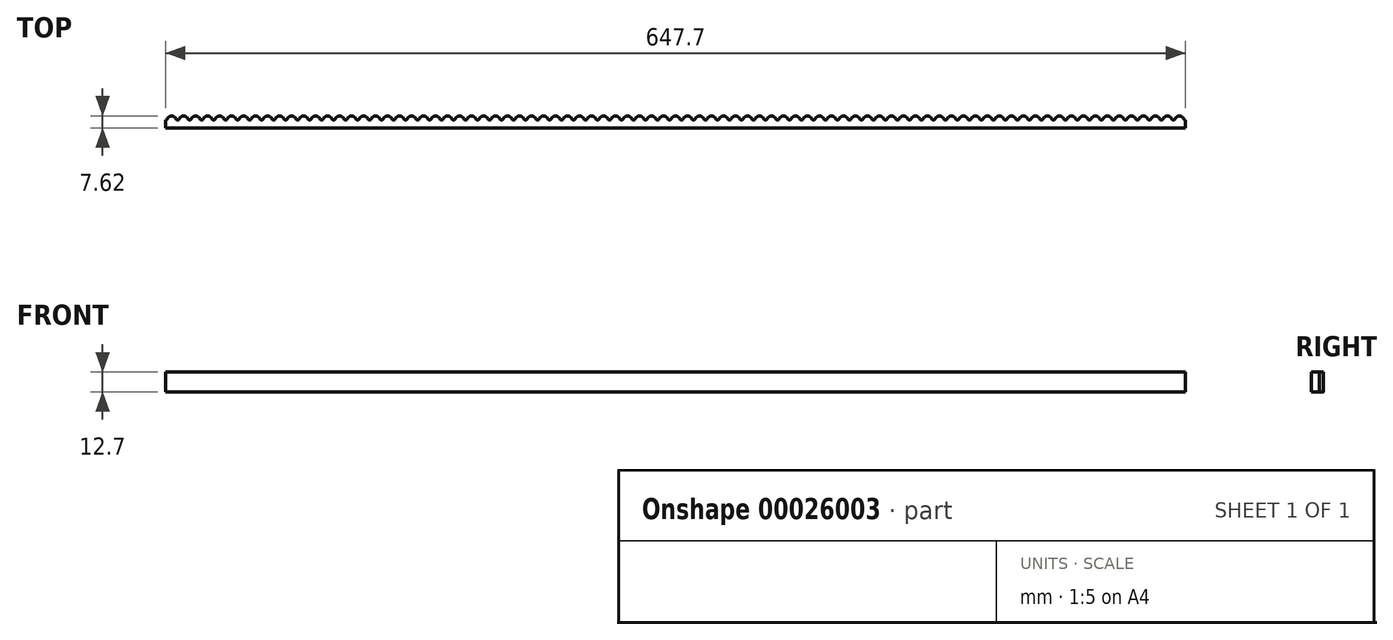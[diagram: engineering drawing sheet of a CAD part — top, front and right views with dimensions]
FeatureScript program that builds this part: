
annotation { "Feature Type Name" : "Feature", "Feature Type Description" : "" }
export const myFeature = defineFeature(function(context is Context, id is Id, definition is map)
    precondition{}
    {
        {
            var Q0;
            Q0=qCreatedBy(makeId("Top.planeOp"),FACE);
            var sketch = newSketch(context, id + "F0", { "sketchPlane" : qUnion([Q0])});
            skLineSegment(sketch, "E0.bottom", {"start": v(0, 0) * mm, "end": v(7.62, 0) * mm});
            skLineSegment(sketch, "E0.top", {"start": v(0, 7.62) * mm, "end": v(7.62, 7.62) * mm, "construction": true});
            skLineSegment(sketch, "E0.left", {"start": v(0, 0) * mm, "end": v(0, 7.62) * mm, "construction": true});
            skLineSegment(sketch, "E0.right", {"start": v(7.62, 0) * mm, "end": v(7.62, 7.62) * mm, "construction": true});
            skLineSegment(sketch, "E1", {"start": v(0, 5.08) * mm, "end": v(7.62, 5.08) * mm, "construction": true});
            skArc(sketch, "E2", {"start": v(0, 5.08) * mm, "mid": v(0.55, 5.21) * mm, "end": v(0.98, 5.58) * mm});
            skArc(sketch, "E3", {"start": v(5.98, 6.5) * mm, "mid": v(3.81, 7.62) * mm, "end": v(1.64, 6.5) * mm});
            skArc(sketch, "E4", {"start": v(6.64, 5.58) * mm, "mid": v(7.07, 5.21) * mm, "end": v(7.62, 5.08) * mm});
            skLineSegment(sketch, "E5", {"start": v(3.8, 5.08) * mm, "end": v(3.8, 7.62) * mm, "construction": true});
            skLineSegment(sketch, "E6", {"start": v(0.98, 5.58) * mm, "end": v(1.64, 6.5) * mm});
            skLineSegment(sketch, "E7", {"start": v(5.98, 6.5) * mm, "end": v(6.64, 5.58) * mm});
            skPoint(sketch, "E8.orphan", {"position": v(1.2, 6.28) * mm});
            skPoint(sketch, "E9.orphan", {"position": v(1.5, 6.28) * mm});
            skPoint(sketch, "E10.orphan", {"position": v(6.12, 6.28) * mm});
            skPoint(sketch, "E11.orphan", {"position": v(6.42, 6.28) * mm});
            skLineSegment(sketch, "E12.1.0.0", {"start": v(7.62, 0) * mm, "end": v(15.24, 0) * mm});
            skArc(sketch, "E12.1.0.1", {"start": v(13.6, 6.5) * mm, "mid": v(11.43, 7.62) * mm, "end": v(9.26, 6.5) * mm});
            skLineSegment(sketch, "E12.1.0.2", {"start": v(13.6, 6.5) * mm, "end": v(14.26, 5.58) * mm});
            skArc(sketch, "E12.1.0.3", {"start": v(7.62, 5.08) * mm, "mid": v(8.17, 5.21) * mm, "end": v(8.6, 5.58) * mm});
            skPoint(sketch, "E12.1.0.4", {"position": v(14.04, 6.28) * mm});
            skLineSegment(sketch, "E12.1.0.5", {"start": v(8.6, 5.58) * mm, "end": v(9.26, 6.5) * mm});
            skArc(sketch, "E12.1.0.6", {"start": v(14.26, 5.58) * mm, "mid": v(14.7, 5.21) * mm, "end": v(15.24, 5.08) * mm});
            skPoint(sketch, "E12.1.0.7", {"position": v(8.82, 6.28) * mm});
            skLineSegment(sketch, "E12.2.0.0", {"start": v(15.24, 0) * mm, "end": v(22.86, 0) * mm});
            skArc(sketch, "E12.2.0.1", {"start": v(21.22, 6.5) * mm, "mid": v(19.05, 7.62) * mm, "end": v(16.88, 6.5) * mm});
            skLineSegment(sketch, "E12.2.0.2", {"start": v(21.22, 6.5) * mm, "end": v(21.88, 5.58) * mm});
            skArc(sketch, "E12.2.0.3", {"start": v(15.24, 5.08) * mm, "mid": v(15.79, 5.21) * mm, "end": v(16.22, 5.58) * mm});
            skPoint(sketch, "E12.2.0.4", {"position": v(21.66, 6.28) * mm});
            skLineSegment(sketch, "E12.2.0.5", {"start": v(16.22, 5.58) * mm, "end": v(16.88, 6.5) * mm});
            skArc(sketch, "E12.2.0.6", {"start": v(21.88, 5.58) * mm, "mid": v(22.31, 5.21) * mm, "end": v(22.86, 5.08) * mm});
            skPoint(sketch, "E12.2.0.7", {"position": v(16.44, 6.28) * mm});
            skLineSegment(sketch, "E12.3.0.0", {"start": v(22.86, 0) * mm, "end": v(30.48, 0) * mm});
            skArc(sketch, "E12.3.0.1", {"start": v(28.84, 6.5) * mm, "mid": v(26.67, 7.62) * mm, "end": v(24.5, 6.5) * mm});
            skLineSegment(sketch, "E12.3.0.2", {"start": v(28.84, 6.5) * mm, "end": v(29.5, 5.58) * mm});
            skArc(sketch, "E12.3.0.3", {"start": v(22.86, 5.08) * mm, "mid": v(23.4, 5.21) * mm, "end": v(23.84, 5.58) * mm});
            skPoint(sketch, "E12.3.0.4", {"position": v(29.28, 6.28) * mm});
            skLineSegment(sketch, "E12.3.0.5", {"start": v(23.84, 5.58) * mm, "end": v(24.5, 6.5) * mm});
            skArc(sketch, "E12.3.0.6", {"start": v(29.5, 5.58) * mm, "mid": v(29.93, 5.21) * mm, "end": v(30.48, 5.08) * mm});
            skPoint(sketch, "E12.3.0.7", {"position": v(24.06, 6.28) * mm});
            skLineSegment(sketch, "E12.4.0.0", {"start": v(30.48, 0) * mm, "end": v(38.1, 0) * mm});
            skArc(sketch, "E12.4.0.1", {"start": v(36.46, 6.5) * mm, "mid": v(34.3, 7.62) * mm, "end": v(32.12, 6.5) * mm});
            skLineSegment(sketch, "E12.4.0.2", {"start": v(36.46, 6.5) * mm, "end": v(37.12, 5.58) * mm});
            skArc(sketch, "E12.4.0.3", {"start": v(30.48, 5.08) * mm, "mid": v(31.03, 5.21) * mm, "end": v(31.46, 5.58) * mm});
            skPoint(sketch, "E12.4.0.4", {"position": v(36.9, 6.28) * mm});
            skLineSegment(sketch, "E12.4.0.5", {"start": v(31.46, 5.58) * mm, "end": v(32.12, 6.5) * mm});
            skArc(sketch, "E12.4.0.6", {"start": v(37.12, 5.58) * mm, "mid": v(37.55, 5.21) * mm, "end": v(38.1, 5.08) * mm});
            skPoint(sketch, "E12.4.0.7", {"position": v(31.68, 6.28) * mm});
            skLineSegment(sketch, "E12.5.0.0", {"start": v(38.1, 0) * mm, "end": v(45.72, 0) * mm});
            skArc(sketch, "E12.5.0.1", {"start": v(44.08, 6.5) * mm, "mid": v(41.91, 7.62) * mm, "end": v(39.74, 6.5) * mm});
            skLineSegment(sketch, "E12.5.0.2", {"start": v(44.08, 6.5) * mm, "end": v(44.74, 5.58) * mm});
            skArc(sketch, "E12.5.0.3", {"start": v(38.1, 5.08) * mm, "mid": v(38.65, 5.21) * mm, "end": v(39.08, 5.58) * mm});
            skPoint(sketch, "E12.5.0.4", {"position": v(44.52, 6.28) * mm});
            skLineSegment(sketch, "E12.5.0.5", {"start": v(39.08, 5.58) * mm, "end": v(39.74, 6.5) * mm});
            skArc(sketch, "E12.5.0.6", {"start": v(44.74, 5.58) * mm, "mid": v(45.17, 5.21) * mm, "end": v(45.72, 5.08) * mm});
            skPoint(sketch, "E12.5.0.7", {"position": v(39.3, 6.28) * mm});
            skLineSegment(sketch, "E12.6.0.0", {"start": v(45.72, 0) * mm, "end": v(53.34, 0) * mm});
            skArc(sketch, "E12.6.0.1", {"start": v(51.7, 6.5) * mm, "mid": v(49.53, 7.62) * mm, "end": v(47.36, 6.5) * mm});
            skLineSegment(sketch, "E12.6.0.2", {"start": v(51.7, 6.5) * mm, "end": v(52.36, 5.58) * mm});
            skArc(sketch, "E12.6.0.3", {"start": v(45.72, 5.08) * mm, "mid": v(46.27, 5.21) * mm, "end": v(46.7, 5.58) * mm});
            skPoint(sketch, "E12.6.0.4", {"position": v(52.14, 6.28) * mm});
            skLineSegment(sketch, "E12.6.0.5", {"start": v(46.7, 5.58) * mm, "end": v(47.36, 6.5) * mm});
            skArc(sketch, "E12.6.0.6", {"start": v(52.36, 5.58) * mm, "mid": v(52.8, 5.21) * mm, "end": v(53.34, 5.08) * mm});
            skPoint(sketch, "E12.6.0.7", {"position": v(46.92, 6.28) * mm});
            skLineSegment(sketch, "E12.7.0.0", {"start": v(53.34, 0) * mm, "end": v(60.96, 0) * mm});
            skArc(sketch, "E12.7.0.1", {"start": v(59.32, 6.5) * mm, "mid": v(57.15, 7.62) * mm, "end": v(54.98, 6.5) * mm});
            skLineSegment(sketch, "E12.7.0.2", {"start": v(59.32, 6.5) * mm, "end": v(59.98, 5.58) * mm});
            skArc(sketch, "E12.7.0.3", {"start": v(53.34, 5.08) * mm, "mid": v(53.89, 5.21) * mm, "end": v(54.32, 5.58) * mm});
            skPoint(sketch, "E12.7.0.4", {"position": v(59.76, 6.28) * mm});
            skLineSegment(sketch, "E12.7.0.5", {"start": v(54.32, 5.58) * mm, "end": v(54.98, 6.5) * mm});
            skArc(sketch, "E12.7.0.6", {"start": v(59.98, 5.58) * mm, "mid": v(60.41, 5.21) * mm, "end": v(60.96, 5.08) * mm});
            skPoint(sketch, "E12.7.0.7", {"position": v(54.54, 6.28) * mm});
            skLineSegment(sketch, "E12.8.0.0", {"start": v(60.96, 0) * mm, "end": v(68.58, 0) * mm});
            skArc(sketch, "E12.8.0.1", {"start": v(66.94, 6.5) * mm, "mid": v(64.77, 7.62) * mm, "end": v(62.6, 6.5) * mm});
            skLineSegment(sketch, "E12.8.0.2", {"start": v(66.94, 6.5) * mm, "end": v(67.6, 5.58) * mm});
            skArc(sketch, "E12.8.0.3", {"start": v(60.96, 5.08) * mm, "mid": v(61.5, 5.21) * mm, "end": v(61.94, 5.58) * mm});
            skPoint(sketch, "E12.8.0.4", {"position": v(67.38, 6.28) * mm});
            skLineSegment(sketch, "E12.8.0.5", {"start": v(61.94, 5.58) * mm, "end": v(62.6, 6.5) * mm});
            skArc(sketch, "E12.8.0.6", {"start": v(67.6, 5.58) * mm, "mid": v(68.03, 5.21) * mm, "end": v(68.58, 5.08) * mm});
            skPoint(sketch, "E12.8.0.7", {"position": v(62.16, 6.28) * mm});
            skLineSegment(sketch, "E12.9.0.0", {"start": v(68.58, 0) * mm, "end": v(76.2, 0) * mm});
            skArc(sketch, "E12.9.0.1", {"start": v(74.56, 6.5) * mm, "mid": v(72.4, 7.62) * mm, "end": v(70.22, 6.5) * mm});
            skLineSegment(sketch, "E12.9.0.2", {"start": v(74.56, 6.5) * mm, "end": v(75.22, 5.58) * mm});
            skArc(sketch, "E12.9.0.3", {"start": v(68.58, 5.08) * mm, "mid": v(69.13, 5.21) * mm, "end": v(69.56, 5.58) * mm});
            skPoint(sketch, "E12.9.0.4", {"position": v(75, 6.28) * mm});
            skLineSegment(sketch, "E12.9.0.5", {"start": v(69.56, 5.58) * mm, "end": v(70.22, 6.5) * mm});
            skArc(sketch, "E12.9.0.6", {"start": v(75.22, 5.58) * mm, "mid": v(75.65, 5.21) * mm, "end": v(76.2, 5.08) * mm});
            skPoint(sketch, "E12.9.0.7", {"position": v(69.78, 6.28) * mm});
            skLineSegment(sketch, "E12.10.0.0", {"start": v(76.2, 0) * mm, "end": v(83.82, 0) * mm});
            skArc(sketch, "E12.10.0.1", {"start": v(82.18, 6.5) * mm, "mid": v(80.01, 7.62) * mm, "end": v(77.84, 6.5) * mm});
            skLineSegment(sketch, "E12.10.0.2", {"start": v(82.18, 6.5) * mm, "end": v(82.84, 5.58) * mm});
            skArc(sketch, "E12.10.0.3", {"start": v(76.2, 5.08) * mm, "mid": v(76.75, 5.21) * mm, "end": v(77.18, 5.58) * mm});
            skPoint(sketch, "E12.10.0.4", {"position": v(82.62, 6.28) * mm});
            skLineSegment(sketch, "E12.10.0.5", {"start": v(77.18, 5.58) * mm, "end": v(77.84, 6.5) * mm});
            skArc(sketch, "E12.10.0.6", {"start": v(82.84, 5.58) * mm, "mid": v(83.27, 5.21) * mm, "end": v(83.82, 5.08) * mm});
            skPoint(sketch, "E12.10.0.7", {"position": v(77.4, 6.28) * mm});
            skLineSegment(sketch, "E12.11.0.0", {"start": v(83.82, 0) * mm, "end": v(91.44, 0) * mm});
            skArc(sketch, "E12.11.0.1", {"start": v(89.8, 6.5) * mm, "mid": v(87.63, 7.62) * mm, "end": v(85.46, 6.5) * mm});
            skLineSegment(sketch, "E12.11.0.2", {"start": v(89.8, 6.5) * mm, "end": v(90.46, 5.58) * mm});
            skArc(sketch, "E12.11.0.3", {"start": v(83.82, 5.08) * mm, "mid": v(84.37, 5.21) * mm, "end": v(84.8, 5.58) * mm});
            skPoint(sketch, "E12.11.0.4", {"position": v(90.24, 6.28) * mm});
            skLineSegment(sketch, "E12.11.0.5", {"start": v(84.8, 5.58) * mm, "end": v(85.46, 6.5) * mm});
            skArc(sketch, "E12.11.0.6", {"start": v(90.46, 5.58) * mm, "mid": v(90.9, 5.21) * mm, "end": v(91.44, 5.08) * mm});
            skPoint(sketch, "E12.11.0.7", {"position": v(85.02, 6.28) * mm});
            skLineSegment(sketch, "E12.12.0.0", {"start": v(91.44, 0) * mm, "end": v(99.06, 0) * mm});
            skArc(sketch, "E12.12.0.1", {"start": v(97.42, 6.5) * mm, "mid": v(95.25, 7.62) * mm, "end": v(93.08, 6.5) * mm});
            skLineSegment(sketch, "E12.12.0.2", {"start": v(97.42, 6.5) * mm, "end": v(98.08, 5.58) * mm});
            skArc(sketch, "E12.12.0.3", {"start": v(91.44, 5.08) * mm, "mid": v(91.99, 5.21) * mm, "end": v(92.42, 5.58) * mm});
            skPoint(sketch, "E12.12.0.4", {"position": v(97.86, 6.28) * mm});
            skLineSegment(sketch, "E12.12.0.5", {"start": v(92.42, 5.58) * mm, "end": v(93.08, 6.5) * mm});
            skArc(sketch, "E12.12.0.6", {"start": v(98.08, 5.58) * mm, "mid": v(98.51, 5.21) * mm, "end": v(99.06, 5.08) * mm});
            skPoint(sketch, "E12.12.0.7", {"position": v(92.64, 6.28) * mm});
            skLineSegment(sketch, "E12.13.0.0", {"start": v(99.06, 0) * mm, "end": v(106.68, 0) * mm});
            skArc(sketch, "E12.13.0.1", {"start": v(105.04, 6.5) * mm, "mid": v(102.87, 7.62) * mm, "end": v(100.7, 6.5) * mm});
            skLineSegment(sketch, "E12.13.0.2", {"start": v(105.04, 6.5) * mm, "end": v(105.7, 5.58) * mm});
            skArc(sketch, "E12.13.0.3", {"start": v(99.06, 5.08) * mm, "mid": v(99.6, 5.21) * mm, "end": v(100.04, 5.58) * mm});
            skPoint(sketch, "E12.13.0.4", {"position": v(105.48, 6.28) * mm});
            skLineSegment(sketch, "E12.13.0.5", {"start": v(100.04, 5.58) * mm, "end": v(100.7, 6.5) * mm});
            skArc(sketch, "E12.13.0.6", {"start": v(105.7, 5.58) * mm, "mid": v(106.13, 5.21) * mm, "end": v(106.68, 5.08) * mm});
            skPoint(sketch, "E12.13.0.7", {"position": v(100.26, 6.28) * mm});
            skLineSegment(sketch, "E12.14.0.0", {"start": v(106.68, 0) * mm, "end": v(114.3, 0) * mm});
            skArc(sketch, "E12.14.0.1", {"start": v(112.66, 6.5) * mm, "mid": v(110.5, 7.62) * mm, "end": v(108.32, 6.5) * mm});
            skLineSegment(sketch, "E12.14.0.2", {"start": v(112.66, 6.5) * mm, "end": v(113.32, 5.58) * mm});
            skArc(sketch, "E12.14.0.3", {"start": v(106.68, 5.08) * mm, "mid": v(107.23, 5.21) * mm, "end": v(107.66, 5.58) * mm});
            skPoint(sketch, "E12.14.0.4", {"position": v(113.1, 6.28) * mm});
            skLineSegment(sketch, "E12.14.0.5", {"start": v(107.66, 5.58) * mm, "end": v(108.32, 6.5) * mm});
            skArc(sketch, "E12.14.0.6", {"start": v(113.32, 5.58) * mm, "mid": v(113.75, 5.21) * mm, "end": v(114.3, 5.08) * mm});
            skPoint(sketch, "E12.14.0.7", {"position": v(107.88, 6.28) * mm});
            skLineSegment(sketch, "E12.15.0.0", {"start": v(114.3, 0) * mm, "end": v(121.92, 0) * mm});
            skArc(sketch, "E12.15.0.1", {"start": v(120.28, 6.5) * mm, "mid": v(118.11, 7.62) * mm, "end": v(115.94, 6.5) * mm});
            skLineSegment(sketch, "E12.15.0.2", {"start": v(120.28, 6.5) * mm, "end": v(120.94, 5.58) * mm});
            skArc(sketch, "E12.15.0.3", {"start": v(114.3, 5.08) * mm, "mid": v(114.85, 5.21) * mm, "end": v(115.28, 5.58) * mm});
            skPoint(sketch, "E12.15.0.4", {"position": v(120.72, 6.28) * mm});
            skLineSegment(sketch, "E12.15.0.5", {"start": v(115.28, 5.58) * mm, "end": v(115.94, 6.5) * mm});
            skArc(sketch, "E12.15.0.6", {"start": v(120.94, 5.58) * mm, "mid": v(121.37, 5.21) * mm, "end": v(121.92, 5.08) * mm});
            skPoint(sketch, "E12.15.0.7", {"position": v(115.5, 6.28) * mm});
            skLineSegment(sketch, "E12.16.0.0", {"start": v(121.92, 0) * mm, "end": v(129.54, 0) * mm});
            skArc(sketch, "E12.16.0.1", {"start": v(127.9, 6.5) * mm, "mid": v(125.73, 7.62) * mm, "end": v(123.56, 6.5) * mm});
            skLineSegment(sketch, "E12.16.0.2", {"start": v(127.9, 6.5) * mm, "end": v(128.56, 5.58) * mm});
            skArc(sketch, "E12.16.0.3", {"start": v(121.92, 5.08) * mm, "mid": v(122.47, 5.21) * mm, "end": v(122.9, 5.58) * mm});
            skPoint(sketch, "E12.16.0.4", {"position": v(128.34, 6.28) * mm});
            skLineSegment(sketch, "E12.16.0.5", {"start": v(122.9, 5.58) * mm, "end": v(123.56, 6.5) * mm});
            skArc(sketch, "E12.16.0.6", {"start": v(128.56, 5.58) * mm, "mid": v(129, 5.21) * mm, "end": v(129.54, 5.08) * mm});
            skPoint(sketch, "E12.16.0.7", {"position": v(123.12, 6.28) * mm});
            skLineSegment(sketch, "E12.17.0.0", {"start": v(129.54, 0) * mm, "end": v(137.16, 0) * mm});
            skArc(sketch, "E12.17.0.1", {"start": v(135.52, 6.5) * mm, "mid": v(133.35, 7.62) * mm, "end": v(131.18, 6.5) * mm});
            skLineSegment(sketch, "E12.17.0.2", {"start": v(135.52, 6.5) * mm, "end": v(136.18, 5.58) * mm});
            skArc(sketch, "E12.17.0.3", {"start": v(129.54, 5.08) * mm, "mid": v(130.09, 5.21) * mm, "end": v(130.52, 5.58) * mm});
            skPoint(sketch, "E12.17.0.4", {"position": v(135.96, 6.28) * mm});
            skLineSegment(sketch, "E12.17.0.5", {"start": v(130.52, 5.58) * mm, "end": v(131.18, 6.5) * mm});
            skArc(sketch, "E12.17.0.6", {"start": v(136.18, 5.58) * mm, "mid": v(136.61, 5.21) * mm, "end": v(137.16, 5.08) * mm});
            skPoint(sketch, "E12.17.0.7", {"position": v(130.74, 6.28) * mm});
            skLineSegment(sketch, "E12.18.0.0", {"start": v(137.16, 0) * mm, "end": v(144.78, 0) * mm});
            skArc(sketch, "E12.18.0.1", {"start": v(143.14, 6.5) * mm, "mid": v(140.97, 7.62) * mm, "end": v(138.8, 6.5) * mm});
            skLineSegment(sketch, "E12.18.0.2", {"start": v(143.14, 6.5) * mm, "end": v(143.8, 5.58) * mm});
            skArc(sketch, "E12.18.0.3", {"start": v(137.16, 5.08) * mm, "mid": v(137.7, 5.21) * mm, "end": v(138.14, 5.58) * mm});
            skPoint(sketch, "E12.18.0.4", {"position": v(143.58, 6.28) * mm});
            skLineSegment(sketch, "E12.18.0.5", {"start": v(138.14, 5.58) * mm, "end": v(138.8, 6.5) * mm});
            skArc(sketch, "E12.18.0.6", {"start": v(143.8, 5.58) * mm, "mid": v(144.23, 5.21) * mm, "end": v(144.78, 5.08) * mm});
            skPoint(sketch, "E12.18.0.7", {"position": v(138.36, 6.28) * mm});
            skLineSegment(sketch, "E12.19.0.0", {"start": v(144.78, 0) * mm, "end": v(152.4, 0) * mm});
            skArc(sketch, "E12.19.0.1", {"start": v(150.76, 6.5) * mm, "mid": v(148.6, 7.62) * mm, "end": v(146.42, 6.5) * mm});
            skLineSegment(sketch, "E12.19.0.2", {"start": v(150.76, 6.5) * mm, "end": v(151.42, 5.58) * mm});
            skArc(sketch, "E12.19.0.3", {"start": v(144.78, 5.08) * mm, "mid": v(145.33, 5.21) * mm, "end": v(145.76, 5.58) * mm});
            skPoint(sketch, "E12.19.0.4", {"position": v(151.2, 6.28) * mm});
            skLineSegment(sketch, "E12.19.0.5", {"start": v(145.76, 5.58) * mm, "end": v(146.42, 6.5) * mm});
            skArc(sketch, "E12.19.0.6", {"start": v(151.42, 5.58) * mm, "mid": v(151.85, 5.21) * mm, "end": v(152.4, 5.08) * mm});
            skPoint(sketch, "E12.19.0.7", {"position": v(145.98, 6.28) * mm});
            skLineSegment(sketch, "E12.direction1", {"start": v(0, 0) * mm, "end": v(7.62, 0) * mm, "construction": true});
            skLineSegment(sketch, "E13.0.20.0", {"start": v(152.4, 0) * mm, "end": v(160.02, 0) * mm});
            skArc(sketch, "E13.3.20.0", {"start": v(158.38, 6.5) * mm, "mid": v(156.21, 7.62) * mm, "end": v(154.04, 6.5) * mm});
            skLineSegment(sketch, "E13.7.20.0", {"start": v(158.38, 6.5) * mm, "end": v(159.04, 5.58) * mm});
            skArc(sketch, "E13.10.20.0", {"start": v(152.4, 5.08) * mm, "mid": v(152.95, 5.21) * mm, "end": v(153.38, 5.58) * mm});
            skPoint(sketch, "E13.14.20.0", {"position": v(158.82, 6.28) * mm});
            skLineSegment(sketch, "E13.15.20.0", {"start": v(153.38, 5.58) * mm, "end": v(154.04, 6.5) * mm});
            skArc(sketch, "E13.18.20.0", {"start": v(159.04, 5.58) * mm, "mid": v(159.47, 5.21) * mm, "end": v(160.02, 5.08) * mm});
            skPoint(sketch, "E13.22.20.0", {"position": v(153.6, 6.28) * mm});
            skLineSegment(sketch, "E13.0.21.0", {"start": v(160.02, 0) * mm, "end": v(167.64, 0) * mm});
            skArc(sketch, "E13.3.21.0", {"start": v(166, 6.5) * mm, "mid": v(163.83, 7.62) * mm, "end": v(161.66, 6.5) * mm});
            skLineSegment(sketch, "E13.7.21.0", {"start": v(166, 6.5) * mm, "end": v(166.66, 5.58) * mm});
            skArc(sketch, "E13.10.21.0", {"start": v(160.02, 5.08) * mm, "mid": v(160.57, 5.21) * mm, "end": v(161, 5.58) * mm});
            skPoint(sketch, "E13.14.21.0", {"position": v(166.44, 6.28) * mm});
            skLineSegment(sketch, "E13.15.21.0", {"start": v(161, 5.58) * mm, "end": v(161.66, 6.5) * mm});
            skArc(sketch, "E13.18.21.0", {"start": v(166.66, 5.58) * mm, "mid": v(167.1, 5.21) * mm, "end": v(167.64, 5.08) * mm});
            skPoint(sketch, "E13.22.21.0", {"position": v(161.22, 6.28) * mm});
            skLineSegment(sketch, "E13.0.22.0", {"start": v(167.64, 0) * mm, "end": v(175.26, 0) * mm});
            skArc(sketch, "E13.3.22.0", {"start": v(173.62, 6.5) * mm, "mid": v(171.45, 7.62) * mm, "end": v(169.28, 6.5) * mm});
            skLineSegment(sketch, "E13.7.22.0", {"start": v(173.62, 6.5) * mm, "end": v(174.28, 5.58) * mm});
            skArc(sketch, "E13.10.22.0", {"start": v(167.64, 5.08) * mm, "mid": v(168.19, 5.21) * mm, "end": v(168.62, 5.58) * mm});
            skPoint(sketch, "E13.14.22.0", {"position": v(174.06, 6.28) * mm});
            skLineSegment(sketch, "E13.15.22.0", {"start": v(168.62, 5.58) * mm, "end": v(169.28, 6.5) * mm});
            skArc(sketch, "E13.18.22.0", {"start": v(174.28, 5.58) * mm, "mid": v(174.71, 5.21) * mm, "end": v(175.26, 5.08) * mm});
            skPoint(sketch, "E13.22.22.0", {"position": v(168.84, 6.28) * mm});
            skLineSegment(sketch, "E13.0.23.0", {"start": v(175.26, 0) * mm, "end": v(182.88, 0) * mm});
            skArc(sketch, "E13.3.23.0", {"start": v(181.24, 6.5) * mm, "mid": v(179.07, 7.62) * mm, "end": v(176.9, 6.5) * mm});
            skLineSegment(sketch, "E13.7.23.0", {"start": v(181.24, 6.5) * mm, "end": v(181.9, 5.58) * mm});
            skArc(sketch, "E13.10.23.0", {"start": v(175.26, 5.08) * mm, "mid": v(175.8, 5.21) * mm, "end": v(176.24, 5.58) * mm});
            skPoint(sketch, "E13.14.23.0", {"position": v(181.68, 6.28) * mm});
            skLineSegment(sketch, "E13.15.23.0", {"start": v(176.24, 5.58) * mm, "end": v(176.9, 6.5) * mm});
            skArc(sketch, "E13.18.23.0", {"start": v(181.9, 5.58) * mm, "mid": v(182.33, 5.21) * mm, "end": v(182.88, 5.08) * mm});
            skPoint(sketch, "E13.22.23.0", {"position": v(176.46, 6.28) * mm});
            skLineSegment(sketch, "E13.0.24.0", {"start": v(182.88, 0) * mm, "end": v(190.5, 0) * mm});
            skArc(sketch, "E13.3.24.0", {"start": v(188.86, 6.5) * mm, "mid": v(186.7, 7.62) * mm, "end": v(184.52, 6.5) * mm});
            skLineSegment(sketch, "E13.7.24.0", {"start": v(188.86, 6.5) * mm, "end": v(189.52, 5.58) * mm});
            skArc(sketch, "E13.10.24.0", {"start": v(182.88, 5.08) * mm, "mid": v(183.43, 5.21) * mm, "end": v(183.86, 5.58) * mm});
            skPoint(sketch, "E13.14.24.0", {"position": v(189.3, 6.28) * mm});
            skLineSegment(sketch, "E13.15.24.0", {"start": v(183.86, 5.58) * mm, "end": v(184.52, 6.5) * mm});
            skArc(sketch, "E13.18.24.0", {"start": v(189.52, 5.58) * mm, "mid": v(189.95, 5.21) * mm, "end": v(190.5, 5.08) * mm});
            skPoint(sketch, "E13.22.24.0", {"position": v(184.08, 6.28) * mm});
            skLineSegment(sketch, "E13.0.25.0", {"start": v(190.5, 0) * mm, "end": v(198.12, 0) * mm});
            skArc(sketch, "E13.3.25.0", {"start": v(196.48, 6.5) * mm, "mid": v(194.3, 7.62) * mm, "end": v(192.14, 6.5) * mm});
            skLineSegment(sketch, "E13.7.25.0", {"start": v(196.48, 6.5) * mm, "end": v(197.14, 5.58) * mm});
            skArc(sketch, "E13.10.25.0", {"start": v(190.5, 5.08) * mm, "mid": v(191.05, 5.21) * mm, "end": v(191.48, 5.58) * mm});
            skPoint(sketch, "E13.14.25.0", {"position": v(196.92, 6.28) * mm});
            skLineSegment(sketch, "E13.15.25.0", {"start": v(191.48, 5.58) * mm, "end": v(192.14, 6.5) * mm});
            skArc(sketch, "E13.18.25.0", {"start": v(197.14, 5.58) * mm, "mid": v(197.57, 5.21) * mm, "end": v(198.12, 5.08) * mm});
            skPoint(sketch, "E13.22.25.0", {"position": v(191.7, 6.28) * mm});
            skLineSegment(sketch, "E13.0.26.0", {"start": v(198.12, 0) * mm, "end": v(205.74, 0) * mm});
            skArc(sketch, "E13.3.26.0", {"start": v(204.1, 6.5) * mm, "mid": v(201.93, 7.62) * mm, "end": v(199.76, 6.5) * mm});
            skLineSegment(sketch, "E13.7.26.0", {"start": v(204.1, 6.5) * mm, "end": v(204.76, 5.58) * mm});
            skArc(sketch, "E13.10.26.0", {"start": v(198.12, 5.08) * mm, "mid": v(198.67, 5.21) * mm, "end": v(199.1, 5.58) * mm});
            skPoint(sketch, "E13.14.26.0", {"position": v(204.54, 6.28) * mm});
            skLineSegment(sketch, "E13.15.26.0", {"start": v(199.1, 5.58) * mm, "end": v(199.76, 6.5) * mm});
            skArc(sketch, "E13.18.26.0", {"start": v(204.76, 5.58) * mm, "mid": v(205.2, 5.21) * mm, "end": v(205.74, 5.08) * mm});
            skPoint(sketch, "E13.22.26.0", {"position": v(199.32, 6.28) * mm});
            skLineSegment(sketch, "E13.0.27.0", {"start": v(205.74, 0) * mm, "end": v(213.36, 0) * mm});
            skArc(sketch, "E13.3.27.0", {"start": v(211.72, 6.5) * mm, "mid": v(209.55, 7.62) * mm, "end": v(207.38, 6.5) * mm});
            skLineSegment(sketch, "E13.7.27.0", {"start": v(211.72, 6.5) * mm, "end": v(212.38, 5.58) * mm});
            skArc(sketch, "E13.10.27.0", {"start": v(205.74, 5.08) * mm, "mid": v(206.29, 5.21) * mm, "end": v(206.72, 5.58) * mm});
            skPoint(sketch, "E13.14.27.0", {"position": v(212.16, 6.28) * mm});
            skLineSegment(sketch, "E13.15.27.0", {"start": v(206.72, 5.58) * mm, "end": v(207.38, 6.5) * mm});
            skArc(sketch, "E13.18.27.0", {"start": v(212.38, 5.58) * mm, "mid": v(212.81, 5.21) * mm, "end": v(213.36, 5.08) * mm});
            skPoint(sketch, "E13.22.27.0", {"position": v(206.94, 6.28) * mm});
            skLineSegment(sketch, "E13.0.28.0", {"start": v(213.36, 0) * mm, "end": v(220.98, 0) * mm});
            skArc(sketch, "E13.3.28.0", {"start": v(219.34, 6.5) * mm, "mid": v(217.17, 7.62) * mm, "end": v(215, 6.5) * mm});
            skLineSegment(sketch, "E13.7.28.0", {"start": v(219.34, 6.5) * mm, "end": v(220, 5.58) * mm});
            skArc(sketch, "E13.10.28.0", {"start": v(213.36, 5.08) * mm, "mid": v(213.9, 5.21) * mm, "end": v(214.34, 5.58) * mm});
            skPoint(sketch, "E13.14.28.0", {"position": v(219.78, 6.28) * mm});
            skLineSegment(sketch, "E13.15.28.0", {"start": v(214.34, 5.58) * mm, "end": v(215, 6.5) * mm});
            skArc(sketch, "E13.18.28.0", {"start": v(220, 5.58) * mm, "mid": v(220.43, 5.21) * mm, "end": v(220.98, 5.08) * mm});
            skPoint(sketch, "E13.22.28.0", {"position": v(214.56, 6.28) * mm});
            skLineSegment(sketch, "E13.0.29.0", {"start": v(220.98, 0) * mm, "end": v(228.6, 0) * mm});
            skArc(sketch, "E13.3.29.0", {"start": v(226.96, 6.5) * mm, "mid": v(224.8, 7.62) * mm, "end": v(222.62, 6.5) * mm});
            skLineSegment(sketch, "E13.7.29.0", {"start": v(226.96, 6.5) * mm, "end": v(227.62, 5.58) * mm});
            skArc(sketch, "E13.10.29.0", {"start": v(220.98, 5.08) * mm, "mid": v(221.53, 5.21) * mm, "end": v(221.96, 5.58) * mm});
            skPoint(sketch, "E13.14.29.0", {"position": v(227.4, 6.28) * mm});
            skLineSegment(sketch, "E13.15.29.0", {"start": v(221.96, 5.58) * mm, "end": v(222.62, 6.5) * mm});
            skArc(sketch, "E13.18.29.0", {"start": v(227.62, 5.58) * mm, "mid": v(228.05, 5.21) * mm, "end": v(228.6, 5.08) * mm});
            skPoint(sketch, "E13.22.29.0", {"position": v(222.18, 6.28) * mm});
            skLineSegment(sketch, "E13.0.30.0", {"start": v(228.6, 0) * mm, "end": v(236.22, 0) * mm});
            skArc(sketch, "E13.3.30.0", {"start": v(234.58, 6.5) * mm, "mid": v(232.4, 7.62) * mm, "end": v(230.24, 6.5) * mm});
            skLineSegment(sketch, "E13.7.30.0", {"start": v(234.58, 6.5) * mm, "end": v(235.24, 5.58) * mm});
            skArc(sketch, "E13.10.30.0", {"start": v(228.6, 5.08) * mm, "mid": v(229.15, 5.21) * mm, "end": v(229.58, 5.58) * mm});
            skPoint(sketch, "E13.14.30.0", {"position": v(235.02, 6.28) * mm});
            skLineSegment(sketch, "E13.15.30.0", {"start": v(229.58, 5.58) * mm, "end": v(230.24, 6.5) * mm});
            skArc(sketch, "E13.18.30.0", {"start": v(235.24, 5.58) * mm, "mid": v(235.67, 5.21) * mm, "end": v(236.22, 5.08) * mm});
            skPoint(sketch, "E13.22.30.0", {"position": v(229.8, 6.28) * mm});
            skLineSegment(sketch, "E13.0.31.0", {"start": v(236.22, 0) * mm, "end": v(243.84, 0) * mm});
            skArc(sketch, "E13.3.31.0", {"start": v(242.2, 6.5) * mm, "mid": v(240.03, 7.62) * mm, "end": v(237.86, 6.5) * mm});
            skLineSegment(sketch, "E13.7.31.0", {"start": v(242.2, 6.5) * mm, "end": v(242.86, 5.58) * mm});
            skArc(sketch, "E13.10.31.0", {"start": v(236.22, 5.08) * mm, "mid": v(236.77, 5.21) * mm, "end": v(237.2, 5.58) * mm});
            skPoint(sketch, "E13.14.31.0", {"position": v(242.64, 6.28) * mm});
            skLineSegment(sketch, "E13.15.31.0", {"start": v(237.2, 5.58) * mm, "end": v(237.86, 6.5) * mm});
            skArc(sketch, "E13.18.31.0", {"start": v(242.86, 5.58) * mm, "mid": v(243.3, 5.21) * mm, "end": v(243.84, 5.08) * mm});
            skPoint(sketch, "E13.22.31.0", {"position": v(237.42, 6.28) * mm});
            skLineSegment(sketch, "E13.0.32.0", {"start": v(243.84, 0) * mm, "end": v(251.46, 0) * mm});
            skArc(sketch, "E13.3.32.0", {"start": v(249.82, 6.5) * mm, "mid": v(247.65, 7.62) * mm, "end": v(245.48, 6.5) * mm});
            skLineSegment(sketch, "E13.7.32.0", {"start": v(249.82, 6.5) * mm, "end": v(250.48, 5.58) * mm});
            skArc(sketch, "E13.10.32.0", {"start": v(243.84, 5.08) * mm, "mid": v(244.39, 5.21) * mm, "end": v(244.82, 5.58) * mm});
            skPoint(sketch, "E13.14.32.0", {"position": v(250.26, 6.28) * mm});
            skLineSegment(sketch, "E13.15.32.0", {"start": v(244.82, 5.58) * mm, "end": v(245.48, 6.5) * mm});
            skArc(sketch, "E13.18.32.0", {"start": v(250.48, 5.58) * mm, "mid": v(250.91, 5.21) * mm, "end": v(251.46, 5.08) * mm});
            skPoint(sketch, "E13.22.32.0", {"position": v(245.04, 6.28) * mm});
            skLineSegment(sketch, "E13.0.33.0", {"start": v(251.46, 0) * mm, "end": v(259.08, 0) * mm});
            skArc(sketch, "E13.3.33.0", {"start": v(257.44, 6.5) * mm, "mid": v(255.27, 7.62) * mm, "end": v(253.1, 6.5) * mm});
            skLineSegment(sketch, "E13.7.33.0", {"start": v(257.44, 6.5) * mm, "end": v(258.1, 5.58) * mm});
            skArc(sketch, "E13.10.33.0", {"start": v(251.46, 5.08) * mm, "mid": v(252, 5.21) * mm, "end": v(252.44, 5.58) * mm});
            skPoint(sketch, "E13.14.33.0", {"position": v(257.88, 6.28) * mm});
            skLineSegment(sketch, "E13.15.33.0", {"start": v(252.44, 5.58) * mm, "end": v(253.1, 6.5) * mm});
            skArc(sketch, "E13.18.33.0", {"start": v(258.1, 5.58) * mm, "mid": v(258.53, 5.21) * mm, "end": v(259.08, 5.08) * mm});
            skPoint(sketch, "E13.22.33.0", {"position": v(252.66, 6.28) * mm});
            skLineSegment(sketch, "E13.0.34.0", {"start": v(259.08, 0) * mm, "end": v(266.7, 0) * mm});
            skArc(sketch, "E13.3.34.0", {"start": v(265.06, 6.5) * mm, "mid": v(262.9, 7.62) * mm, "end": v(260.72, 6.5) * mm});
            skLineSegment(sketch, "E13.7.34.0", {"start": v(265.06, 6.5) * mm, "end": v(265.72, 5.58) * mm});
            skArc(sketch, "E13.10.34.0", {"start": v(259.08, 5.08) * mm, "mid": v(259.63, 5.21) * mm, "end": v(260.06, 5.58) * mm});
            skPoint(sketch, "E13.14.34.0", {"position": v(265.5, 6.28) * mm});
            skLineSegment(sketch, "E13.15.34.0", {"start": v(260.06, 5.58) * mm, "end": v(260.72, 6.5) * mm});
            skArc(sketch, "E13.18.34.0", {"start": v(265.72, 5.58) * mm, "mid": v(266.15, 5.21) * mm, "end": v(266.7, 5.08) * mm});
            skPoint(sketch, "E13.22.34.0", {"position": v(260.28, 6.28) * mm});
            skLineSegment(sketch, "E13.0.35.0", {"start": v(266.7, 0) * mm, "end": v(274.32, 0) * mm});
            skArc(sketch, "E13.3.35.0", {"start": v(272.68, 6.5) * mm, "mid": v(270.51, 7.62) * mm, "end": v(268.34, 6.5) * mm});
            skLineSegment(sketch, "E13.7.35.0", {"start": v(272.68, 6.5) * mm, "end": v(273.34, 5.58) * mm});
            skArc(sketch, "E13.10.35.0", {"start": v(266.7, 5.08) * mm, "mid": v(267.25, 5.21) * mm, "end": v(267.68, 5.58) * mm});
            skPoint(sketch, "E13.14.35.0", {"position": v(273.12, 6.28) * mm});
            skLineSegment(sketch, "E13.15.35.0", {"start": v(267.68, 5.58) * mm, "end": v(268.34, 6.5) * mm});
            skArc(sketch, "E13.18.35.0", {"start": v(273.34, 5.58) * mm, "mid": v(273.77, 5.21) * mm, "end": v(274.32, 5.08) * mm});
            skPoint(sketch, "E13.22.35.0", {"position": v(267.9, 6.28) * mm});
            skLineSegment(sketch, "E13.0.36.0", {"start": v(274.32, 0) * mm, "end": v(281.94, 0) * mm});
            skArc(sketch, "E13.3.36.0", {"start": v(280.3, 6.5) * mm, "mid": v(278.13, 7.62) * mm, "end": v(275.96, 6.5) * mm});
            skLineSegment(sketch, "E13.7.36.0", {"start": v(280.3, 6.5) * mm, "end": v(280.96, 5.58) * mm});
            skArc(sketch, "E13.10.36.0", {"start": v(274.32, 5.08) * mm, "mid": v(274.87, 5.21) * mm, "end": v(275.3, 5.58) * mm});
            skPoint(sketch, "E13.14.36.0", {"position": v(280.74, 6.28) * mm});
            skLineSegment(sketch, "E13.15.36.0", {"start": v(275.3, 5.58) * mm, "end": v(275.96, 6.5) * mm});
            skArc(sketch, "E13.18.36.0", {"start": v(280.96, 5.58) * mm, "mid": v(281.4, 5.21) * mm, "end": v(281.94, 5.08) * mm});
            skPoint(sketch, "E13.22.36.0", {"position": v(275.52, 6.28) * mm});
            skLineSegment(sketch, "E13.0.37.0", {"start": v(281.94, 0) * mm, "end": v(289.56, 0) * mm});
            skArc(sketch, "E13.3.37.0", {"start": v(287.92, 6.5) * mm, "mid": v(285.75, 7.62) * mm, "end": v(283.58, 6.5) * mm});
            skLineSegment(sketch, "E13.7.37.0", {"start": v(287.92, 6.5) * mm, "end": v(288.58, 5.58) * mm});
            skArc(sketch, "E13.10.37.0", {"start": v(281.94, 5.08) * mm, "mid": v(282.49, 5.21) * mm, "end": v(282.92, 5.58) * mm});
            skPoint(sketch, "E13.14.37.0", {"position": v(288.36, 6.28) * mm});
            skLineSegment(sketch, "E13.15.37.0", {"start": v(282.92, 5.58) * mm, "end": v(283.58, 6.5) * mm});
            skArc(sketch, "E13.18.37.0", {"start": v(288.58, 5.58) * mm, "mid": v(289.01, 5.21) * mm, "end": v(289.56, 5.08) * mm});
            skPoint(sketch, "E13.22.37.0", {"position": v(283.14, 6.28) * mm});
            skLineSegment(sketch, "E13.0.38.0", {"start": v(289.56, 0) * mm, "end": v(297.18, 0) * mm});
            skArc(sketch, "E13.3.38.0", {"start": v(295.54, 6.5) * mm, "mid": v(293.37, 7.62) * mm, "end": v(291.2, 6.5) * mm});
            skLineSegment(sketch, "E13.7.38.0", {"start": v(295.54, 6.5) * mm, "end": v(296.2, 5.58) * mm});
            skArc(sketch, "E13.10.38.0", {"start": v(289.56, 5.08) * mm, "mid": v(290.1, 5.21) * mm, "end": v(290.54, 5.58) * mm});
            skPoint(sketch, "E13.14.38.0", {"position": v(295.98, 6.28) * mm});
            skLineSegment(sketch, "E13.15.38.0", {"start": v(290.54, 5.58) * mm, "end": v(291.2, 6.5) * mm});
            skArc(sketch, "E13.18.38.0", {"start": v(296.2, 5.58) * mm, "mid": v(296.63, 5.21) * mm, "end": v(297.18, 5.08) * mm});
            skPoint(sketch, "E13.22.38.0", {"position": v(290.76, 6.28) * mm});
            skLineSegment(sketch, "E13.0.39.0", {"start": v(297.18, 0) * mm, "end": v(304.8, 0) * mm});
            skArc(sketch, "E13.3.39.0", {"start": v(303.16, 6.5) * mm, "mid": v(301, 7.62) * mm, "end": v(298.82, 6.5) * mm});
            skLineSegment(sketch, "E13.7.39.0", {"start": v(303.16, 6.5) * mm, "end": v(303.82, 5.58) * mm});
            skArc(sketch, "E13.10.39.0", {"start": v(297.18, 5.08) * mm, "mid": v(297.73, 5.21) * mm, "end": v(298.16, 5.58) * mm});
            skPoint(sketch, "E13.14.39.0", {"position": v(303.6, 6.28) * mm});
            skLineSegment(sketch, "E13.15.39.0", {"start": v(298.16, 5.58) * mm, "end": v(298.82, 6.5) * mm});
            skArc(sketch, "E13.18.39.0", {"start": v(303.82, 5.58) * mm, "mid": v(304.25, 5.21) * mm, "end": v(304.8, 5.08) * mm});
            skPoint(sketch, "E13.22.39.0", {"position": v(298.38, 6.28) * mm});
            skLineSegment(sketch, "E13.0.40.0", {"start": v(304.8, 0) * mm, "end": v(312.42, 0) * mm});
            skArc(sketch, "E13.3.40.0", {"start": v(310.78, 6.5) * mm, "mid": v(308.61, 7.62) * mm, "end": v(306.44, 6.5) * mm});
            skLineSegment(sketch, "E13.7.40.0", {"start": v(310.78, 6.5) * mm, "end": v(311.44, 5.58) * mm});
            skArc(sketch, "E13.10.40.0", {"start": v(304.8, 5.08) * mm, "mid": v(305.35, 5.21) * mm, "end": v(305.78, 5.58) * mm});
            skPoint(sketch, "E13.14.40.0", {"position": v(311.22, 6.28) * mm});
            skLineSegment(sketch, "E13.15.40.0", {"start": v(305.78, 5.58) * mm, "end": v(306.44, 6.5) * mm});
            skArc(sketch, "E13.18.40.0", {"start": v(311.44, 5.58) * mm, "mid": v(311.87, 5.21) * mm, "end": v(312.42, 5.08) * mm});
            skPoint(sketch, "E13.22.40.0", {"position": v(306, 6.28) * mm});
            skLineSegment(sketch, "E13.0.41.0", {"start": v(312.42, 0) * mm, "end": v(320.04, 0) * mm});
            skArc(sketch, "E13.3.41.0", {"start": v(318.4, 6.5) * mm, "mid": v(316.23, 7.62) * mm, "end": v(314.06, 6.5) * mm});
            skLineSegment(sketch, "E13.7.41.0", {"start": v(318.4, 6.5) * mm, "end": v(319.06, 5.58) * mm});
            skArc(sketch, "E13.10.41.0", {"start": v(312.42, 5.08) * mm, "mid": v(312.97, 5.21) * mm, "end": v(313.4, 5.58) * mm});
            skPoint(sketch, "E13.14.41.0", {"position": v(318.84, 6.28) * mm});
            skLineSegment(sketch, "E13.15.41.0", {"start": v(313.4, 5.58) * mm, "end": v(314.06, 6.5) * mm});
            skArc(sketch, "E13.18.41.0", {"start": v(319.06, 5.58) * mm, "mid": v(319.5, 5.21) * mm, "end": v(320.04, 5.08) * mm});
            skPoint(sketch, "E13.22.41.0", {"position": v(313.62, 6.28) * mm});
            skLineSegment(sketch, "E13.0.42.0", {"start": v(320.04, 0) * mm, "end": v(327.66, 0) * mm});
            skArc(sketch, "E13.3.42.0", {"start": v(326.02, 6.5) * mm, "mid": v(323.85, 7.62) * mm, "end": v(321.68, 6.5) * mm});
            skLineSegment(sketch, "E13.7.42.0", {"start": v(326.02, 6.5) * mm, "end": v(326.68, 5.58) * mm});
            skArc(sketch, "E13.10.42.0", {"start": v(320.04, 5.08) * mm, "mid": v(320.59, 5.21) * mm, "end": v(321.02, 5.58) * mm});
            skPoint(sketch, "E13.14.42.0", {"position": v(326.46, 6.28) * mm});
            skLineSegment(sketch, "E13.15.42.0", {"start": v(321.02, 5.58) * mm, "end": v(321.68, 6.5) * mm});
            skArc(sketch, "E13.18.42.0", {"start": v(326.68, 5.58) * mm, "mid": v(327.11, 5.21) * mm, "end": v(327.66, 5.08) * mm});
            skPoint(sketch, "E13.22.42.0", {"position": v(321.24, 6.28) * mm});
            skLineSegment(sketch, "E13.0.43.0", {"start": v(327.66, 0) * mm, "end": v(335.28, 0) * mm});
            skArc(sketch, "E13.3.43.0", {"start": v(333.64, 6.5) * mm, "mid": v(331.47, 7.62) * mm, "end": v(329.3, 6.5) * mm});
            skLineSegment(sketch, "E13.7.43.0", {"start": v(333.64, 6.5) * mm, "end": v(334.3, 5.58) * mm});
            skArc(sketch, "E13.10.43.0", {"start": v(327.66, 5.08) * mm, "mid": v(328.2, 5.21) * mm, "end": v(328.64, 5.58) * mm});
            skPoint(sketch, "E13.14.43.0", {"position": v(334.08, 6.28) * mm});
            skLineSegment(sketch, "E13.15.43.0", {"start": v(328.64, 5.58) * mm, "end": v(329.3, 6.5) * mm});
            skArc(sketch, "E13.18.43.0", {"start": v(334.3, 5.58) * mm, "mid": v(334.73, 5.21) * mm, "end": v(335.28, 5.08) * mm});
            skPoint(sketch, "E13.22.43.0", {"position": v(328.86, 6.28) * mm});
            skLineSegment(sketch, "E13.0.44.0", {"start": v(335.28, 0) * mm, "end": v(342.9, 0) * mm});
            skArc(sketch, "E13.3.44.0", {"start": v(341.26, 6.5) * mm, "mid": v(339.1, 7.62) * mm, "end": v(336.92, 6.5) * mm});
            skLineSegment(sketch, "E13.7.44.0", {"start": v(341.26, 6.5) * mm, "end": v(341.92, 5.58) * mm});
            skArc(sketch, "E13.10.44.0", {"start": v(335.28, 5.08) * mm, "mid": v(335.83, 5.21) * mm, "end": v(336.26, 5.58) * mm});
            skPoint(sketch, "E13.14.44.0", {"position": v(341.7, 6.28) * mm});
            skLineSegment(sketch, "E13.15.44.0", {"start": v(336.26, 5.58) * mm, "end": v(336.92, 6.5) * mm});
            skArc(sketch, "E13.18.44.0", {"start": v(341.92, 5.58) * mm, "mid": v(342.35, 5.21) * mm, "end": v(342.9, 5.08) * mm});
            skPoint(sketch, "E13.22.44.0", {"position": v(336.48, 6.28) * mm});
            skLineSegment(sketch, "E13.0.45.0", {"start": v(342.9, 0) * mm, "end": v(350.52, 0) * mm});
            skArc(sketch, "E13.3.45.0", {"start": v(348.88, 6.5) * mm, "mid": v(346.71, 7.62) * mm, "end": v(344.54, 6.5) * mm});
            skLineSegment(sketch, "E13.7.45.0", {"start": v(348.88, 6.5) * mm, "end": v(349.54, 5.58) * mm});
            skArc(sketch, "E13.10.45.0", {"start": v(342.9, 5.08) * mm, "mid": v(343.45, 5.21) * mm, "end": v(343.88, 5.58) * mm});
            skPoint(sketch, "E13.14.45.0", {"position": v(349.32, 6.28) * mm});
            skLineSegment(sketch, "E13.15.45.0", {"start": v(343.88, 5.58) * mm, "end": v(344.54, 6.5) * mm});
            skArc(sketch, "E13.18.45.0", {"start": v(349.54, 5.58) * mm, "mid": v(349.97, 5.21) * mm, "end": v(350.52, 5.08) * mm});
            skPoint(sketch, "E13.22.45.0", {"position": v(344.1, 6.28) * mm});
            skLineSegment(sketch, "E13.0.46.0", {"start": v(350.52, 0) * mm, "end": v(358.14, 0) * mm});
            skArc(sketch, "E13.3.46.0", {"start": v(356.5, 6.5) * mm, "mid": v(354.33, 7.62) * mm, "end": v(352.16, 6.5) * mm});
            skLineSegment(sketch, "E13.7.46.0", {"start": v(356.5, 6.5) * mm, "end": v(357.16, 5.58) * mm});
            skArc(sketch, "E13.10.46.0", {"start": v(350.52, 5.08) * mm, "mid": v(351.07, 5.21) * mm, "end": v(351.5, 5.58) * mm});
            skPoint(sketch, "E13.14.46.0", {"position": v(356.94, 6.28) * mm});
            skLineSegment(sketch, "E13.15.46.0", {"start": v(351.5, 5.58) * mm, "end": v(352.16, 6.5) * mm});
            skArc(sketch, "E13.18.46.0", {"start": v(357.16, 5.58) * mm, "mid": v(357.6, 5.21) * mm, "end": v(358.14, 5.08) * mm});
            skPoint(sketch, "E13.22.46.0", {"position": v(351.72, 6.28) * mm});
            skLineSegment(sketch, "E13.0.47.0", {"start": v(358.14, 0) * mm, "end": v(365.76, 0) * mm});
            skArc(sketch, "E13.3.47.0", {"start": v(364.12, 6.5) * mm, "mid": v(361.95, 7.62) * mm, "end": v(359.78, 6.5) * mm});
            skLineSegment(sketch, "E13.7.47.0", {"start": v(364.12, 6.5) * mm, "end": v(364.78, 5.58) * mm});
            skArc(sketch, "E13.10.47.0", {"start": v(358.14, 5.08) * mm, "mid": v(358.69, 5.21) * mm, "end": v(359.12, 5.58) * mm});
            skPoint(sketch, "E13.14.47.0", {"position": v(364.56, 6.28) * mm});
            skLineSegment(sketch, "E13.15.47.0", {"start": v(359.12, 5.58) * mm, "end": v(359.78, 6.5) * mm});
            skArc(sketch, "E13.18.47.0", {"start": v(364.78, 5.58) * mm, "mid": v(365.21, 5.21) * mm, "end": v(365.76, 5.08) * mm});
            skPoint(sketch, "E13.22.47.0", {"position": v(359.34, 6.28) * mm});
            skLineSegment(sketch, "E13.0.48.0", {"start": v(365.76, 0) * mm, "end": v(373.38, 0) * mm});
            skArc(sketch, "E13.3.48.0", {"start": v(371.74, 6.5) * mm, "mid": v(369.57, 7.62) * mm, "end": v(367.4, 6.5) * mm});
            skLineSegment(sketch, "E13.7.48.0", {"start": v(371.74, 6.5) * mm, "end": v(372.4, 5.58) * mm});
            skArc(sketch, "E13.10.48.0", {"start": v(365.76, 5.08) * mm, "mid": v(366.3, 5.21) * mm, "end": v(366.74, 5.58) * mm});
            skPoint(sketch, "E13.14.48.0", {"position": v(372.18, 6.28) * mm});
            skLineSegment(sketch, "E13.15.48.0", {"start": v(366.74, 5.58) * mm, "end": v(367.4, 6.5) * mm});
            skArc(sketch, "E13.18.48.0", {"start": v(372.4, 5.58) * mm, "mid": v(372.83, 5.21) * mm, "end": v(373.38, 5.08) * mm});
            skPoint(sketch, "E13.22.48.0", {"position": v(366.96, 6.28) * mm});
            skLineSegment(sketch, "E13.0.49.0", {"start": v(373.38, 0) * mm, "end": v(381, 0) * mm});
            skArc(sketch, "E13.3.49.0", {"start": v(379.36, 6.5) * mm, "mid": v(377.2, 7.62) * mm, "end": v(375.02, 6.5) * mm});
            skLineSegment(sketch, "E13.7.49.0", {"start": v(379.36, 6.5) * mm, "end": v(380.02, 5.58) * mm});
            skArc(sketch, "E13.10.49.0", {"start": v(373.38, 5.08) * mm, "mid": v(373.93, 5.21) * mm, "end": v(374.36, 5.58) * mm});
            skPoint(sketch, "E13.14.49.0", {"position": v(379.8, 6.28) * mm});
            skLineSegment(sketch, "E13.15.49.0", {"start": v(374.36, 5.58) * mm, "end": v(375.02, 6.5) * mm});
            skArc(sketch, "E13.18.49.0", {"start": v(380.02, 5.58) * mm, "mid": v(380.45, 5.21) * mm, "end": v(381, 5.08) * mm});
            skPoint(sketch, "E13.22.49.0", {"position": v(374.58, 6.28) * mm});
            skLineSegment(sketch, "E14.0.50.0", {"start": v(381, 0) * mm, "end": v(388.62, 0) * mm});
            skArc(sketch, "E14.3.50.0", {"start": v(386.98, 6.5) * mm, "mid": v(384.81, 7.62) * mm, "end": v(382.64, 6.5) * mm});
            skLineSegment(sketch, "E14.7.50.0", {"start": v(386.98, 6.5) * mm, "end": v(387.64, 5.58) * mm});
            skArc(sketch, "E14.10.50.0", {"start": v(381, 5.08) * mm, "mid": v(381.55, 5.21) * mm, "end": v(381.98, 5.58) * mm});
            skPoint(sketch, "E14.14.50.0", {"position": v(387.42, 6.28) * mm});
            skLineSegment(sketch, "E14.15.50.0", {"start": v(381.98, 5.58) * mm, "end": v(382.64, 6.5) * mm});
            skArc(sketch, "E14.18.50.0", {"start": v(387.64, 5.58) * mm, "mid": v(388.07, 5.21) * mm, "end": v(388.62, 5.08) * mm});
            skPoint(sketch, "E14.22.50.0", {"position": v(382.2, 6.28) * mm});
            skLineSegment(sketch, "E14.0.51.0", {"start": v(388.62, 0) * mm, "end": v(396.24, 0) * mm});
            skArc(sketch, "E14.3.51.0", {"start": v(394.6, 6.5) * mm, "mid": v(392.43, 7.62) * mm, "end": v(390.26, 6.5) * mm});
            skLineSegment(sketch, "E14.7.51.0", {"start": v(394.6, 6.5) * mm, "end": v(395.26, 5.58) * mm});
            skArc(sketch, "E14.10.51.0", {"start": v(388.62, 5.08) * mm, "mid": v(389.17, 5.21) * mm, "end": v(389.6, 5.58) * mm});
            skPoint(sketch, "E14.14.51.0", {"position": v(395.04, 6.28) * mm});
            skLineSegment(sketch, "E14.15.51.0", {"start": v(389.6, 5.58) * mm, "end": v(390.26, 6.5) * mm});
            skArc(sketch, "E14.18.51.0", {"start": v(395.26, 5.58) * mm, "mid": v(395.7, 5.21) * mm, "end": v(396.24, 5.08) * mm});
            skPoint(sketch, "E14.22.51.0", {"position": v(389.82, 6.28) * mm});
            skLineSegment(sketch, "E14.0.52.0", {"start": v(396.24, 0) * mm, "end": v(403.86, 0) * mm});
            skArc(sketch, "E14.3.52.0", {"start": v(402.22, 6.5) * mm, "mid": v(400.05, 7.62) * mm, "end": v(397.88, 6.5) * mm});
            skLineSegment(sketch, "E14.7.52.0", {"start": v(402.22, 6.5) * mm, "end": v(402.88, 5.58) * mm});
            skArc(sketch, "E14.10.52.0", {"start": v(396.24, 5.08) * mm, "mid": v(396.79, 5.21) * mm, "end": v(397.22, 5.58) * mm});
            skPoint(sketch, "E14.14.52.0", {"position": v(402.66, 6.28) * mm});
            skLineSegment(sketch, "E14.15.52.0", {"start": v(397.22, 5.58) * mm, "end": v(397.88, 6.5) * mm});
            skArc(sketch, "E14.18.52.0", {"start": v(402.88, 5.58) * mm, "mid": v(403.31, 5.21) * mm, "end": v(403.86, 5.08) * mm});
            skPoint(sketch, "E14.22.52.0", {"position": v(397.44, 6.28) * mm});
            skLineSegment(sketch, "E14.0.53.0", {"start": v(403.86, 0) * mm, "end": v(411.48, 0) * mm});
            skArc(sketch, "E14.3.53.0", {"start": v(409.84, 6.5) * mm, "mid": v(407.67, 7.62) * mm, "end": v(405.5, 6.5) * mm});
            skLineSegment(sketch, "E14.7.53.0", {"start": v(409.84, 6.5) * mm, "end": v(410.5, 5.58) * mm});
            skArc(sketch, "E14.10.53.0", {"start": v(403.86, 5.08) * mm, "mid": v(404.4, 5.21) * mm, "end": v(404.84, 5.58) * mm});
            skPoint(sketch, "E14.14.53.0", {"position": v(410.28, 6.28) * mm});
            skLineSegment(sketch, "E14.15.53.0", {"start": v(404.84, 5.58) * mm, "end": v(405.5, 6.5) * mm});
            skArc(sketch, "E14.18.53.0", {"start": v(410.5, 5.58) * mm, "mid": v(410.93, 5.21) * mm, "end": v(411.48, 5.08) * mm});
            skPoint(sketch, "E14.22.53.0", {"position": v(405.06, 6.28) * mm});
            skLineSegment(sketch, "E14.0.54.0", {"start": v(411.48, 0) * mm, "end": v(419.1, 0) * mm});
            skArc(sketch, "E14.3.54.0", {"start": v(417.46, 6.5) * mm, "mid": v(415.3, 7.62) * mm, "end": v(413.12, 6.5) * mm});
            skLineSegment(sketch, "E14.7.54.0", {"start": v(417.46, 6.5) * mm, "end": v(418.12, 5.58) * mm});
            skArc(sketch, "E14.10.54.0", {"start": v(411.48, 5.08) * mm, "mid": v(412.03, 5.21) * mm, "end": v(412.46, 5.58) * mm});
            skPoint(sketch, "E14.14.54.0", {"position": v(417.9, 6.28) * mm});
            skLineSegment(sketch, "E14.15.54.0", {"start": v(412.46, 5.58) * mm, "end": v(413.12, 6.5) * mm});
            skArc(sketch, "E14.18.54.0", {"start": v(418.12, 5.58) * mm, "mid": v(418.55, 5.21) * mm, "end": v(419.1, 5.08) * mm});
            skPoint(sketch, "E14.22.54.0", {"position": v(412.68, 6.28) * mm});
            skLineSegment(sketch, "E14.0.55.0", {"start": v(419.1, 0) * mm, "end": v(426.72, 0) * mm});
            skArc(sketch, "E14.3.55.0", {"start": v(425.08, 6.5) * mm, "mid": v(422.91, 7.62) * mm, "end": v(420.74, 6.5) * mm});
            skLineSegment(sketch, "E14.7.55.0", {"start": v(425.08, 6.5) * mm, "end": v(425.74, 5.58) * mm});
            skArc(sketch, "E14.10.55.0", {"start": v(419.1, 5.08) * mm, "mid": v(419.65, 5.21) * mm, "end": v(420.08, 5.58) * mm});
            skPoint(sketch, "E14.14.55.0", {"position": v(425.52, 6.28) * mm});
            skLineSegment(sketch, "E14.15.55.0", {"start": v(420.08, 5.58) * mm, "end": v(420.74, 6.5) * mm});
            skArc(sketch, "E14.18.55.0", {"start": v(425.74, 5.58) * mm, "mid": v(426.17, 5.21) * mm, "end": v(426.72, 5.08) * mm});
            skPoint(sketch, "E14.22.55.0", {"position": v(420.3, 6.28) * mm});
            skLineSegment(sketch, "E14.0.56.0", {"start": v(426.72, 0) * mm, "end": v(434.34, 0) * mm});
            skArc(sketch, "E14.3.56.0", {"start": v(432.7, 6.5) * mm, "mid": v(430.53, 7.62) * mm, "end": v(428.36, 6.5) * mm});
            skLineSegment(sketch, "E14.7.56.0", {"start": v(432.7, 6.5) * mm, "end": v(433.36, 5.58) * mm});
            skArc(sketch, "E14.10.56.0", {"start": v(426.72, 5.08) * mm, "mid": v(427.27, 5.21) * mm, "end": v(427.7, 5.58) * mm});
            skPoint(sketch, "E14.14.56.0", {"position": v(433.14, 6.28) * mm});
            skLineSegment(sketch, "E14.15.56.0", {"start": v(427.7, 5.58) * mm, "end": v(428.36, 6.5) * mm});
            skArc(sketch, "E14.18.56.0", {"start": v(433.36, 5.58) * mm, "mid": v(433.8, 5.21) * mm, "end": v(434.34, 5.08) * mm});
            skPoint(sketch, "E14.22.56.0", {"position": v(427.92, 6.28) * mm});
            skLineSegment(sketch, "E14.0.57.0", {"start": v(434.34, 0) * mm, "end": v(441.96, 0) * mm});
            skArc(sketch, "E14.3.57.0", {"start": v(440.32, 6.5) * mm, "mid": v(438.15, 7.62) * mm, "end": v(435.98, 6.5) * mm});
            skLineSegment(sketch, "E14.7.57.0", {"start": v(440.32, 6.5) * mm, "end": v(440.98, 5.58) * mm});
            skArc(sketch, "E14.10.57.0", {"start": v(434.34, 5.08) * mm, "mid": v(434.89, 5.21) * mm, "end": v(435.32, 5.58) * mm});
            skPoint(sketch, "E14.14.57.0", {"position": v(440.76, 6.28) * mm});
            skLineSegment(sketch, "E14.15.57.0", {"start": v(435.32, 5.58) * mm, "end": v(435.98, 6.5) * mm});
            skArc(sketch, "E14.18.57.0", {"start": v(440.98, 5.58) * mm, "mid": v(441.41, 5.21) * mm, "end": v(441.96, 5.08) * mm});
            skPoint(sketch, "E14.22.57.0", {"position": v(435.54, 6.28) * mm});
            skLineSegment(sketch, "E14.0.58.0", {"start": v(441.96, 0) * mm, "end": v(449.58, 0) * mm});
            skArc(sketch, "E14.3.58.0", {"start": v(447.94, 6.5) * mm, "mid": v(445.77, 7.62) * mm, "end": v(443.6, 6.5) * mm});
            skLineSegment(sketch, "E14.7.58.0", {"start": v(447.94, 6.5) * mm, "end": v(448.6, 5.58) * mm});
            skArc(sketch, "E14.10.58.0", {"start": v(441.96, 5.08) * mm, "mid": v(442.5, 5.21) * mm, "end": v(442.94, 5.58) * mm});
            skPoint(sketch, "E14.14.58.0", {"position": v(448.38, 6.28) * mm});
            skLineSegment(sketch, "E14.15.58.0", {"start": v(442.94, 5.58) * mm, "end": v(443.6, 6.5) * mm});
            skArc(sketch, "E14.18.58.0", {"start": v(448.6, 5.58) * mm, "mid": v(449.03, 5.21) * mm, "end": v(449.58, 5.08) * mm});
            skPoint(sketch, "E14.22.58.0", {"position": v(443.16, 6.28) * mm});
            skLineSegment(sketch, "E14.0.59.0", {"start": v(449.58, 0) * mm, "end": v(457.2, 0) * mm});
            skArc(sketch, "E14.3.59.0", {"start": v(455.56, 6.5) * mm, "mid": v(453.4, 7.62) * mm, "end": v(451.22, 6.5) * mm});
            skLineSegment(sketch, "E14.7.59.0", {"start": v(455.56, 6.5) * mm, "end": v(456.22, 5.58) * mm});
            skArc(sketch, "E14.10.59.0", {"start": v(449.58, 5.08) * mm, "mid": v(450.13, 5.21) * mm, "end": v(450.56, 5.58) * mm});
            skPoint(sketch, "E14.14.59.0", {"position": v(456, 6.28) * mm});
            skLineSegment(sketch, "E14.15.59.0", {"start": v(450.56, 5.58) * mm, "end": v(451.22, 6.5) * mm});
            skArc(sketch, "E14.18.59.0", {"start": v(456.22, 5.58) * mm, "mid": v(456.65, 5.21) * mm, "end": v(457.2, 5.08) * mm});
            skPoint(sketch, "E14.22.59.0", {"position": v(450.78, 6.28) * mm});
            skLineSegment(sketch, "E14.0.60.0", {"start": v(457.2, 0) * mm, "end": v(464.82, 0) * mm});
            skArc(sketch, "E14.3.60.0", {"start": v(463.18, 6.5) * mm, "mid": v(461.01, 7.62) * mm, "end": v(458.84, 6.5) * mm});
            skLineSegment(sketch, "E14.7.60.0", {"start": v(463.18, 6.5) * mm, "end": v(463.84, 5.58) * mm});
            skArc(sketch, "E14.10.60.0", {"start": v(457.2, 5.08) * mm, "mid": v(457.75, 5.21) * mm, "end": v(458.18, 5.58) * mm});
            skPoint(sketch, "E14.14.60.0", {"position": v(463.62, 6.28) * mm});
            skLineSegment(sketch, "E14.15.60.0", {"start": v(458.18, 5.58) * mm, "end": v(458.84, 6.5) * mm});
            skArc(sketch, "E14.18.60.0", {"start": v(463.84, 5.58) * mm, "mid": v(464.27, 5.21) * mm, "end": v(464.82, 5.08) * mm});
            skPoint(sketch, "E14.22.60.0", {"position": v(458.4, 6.28) * mm});
            skLineSegment(sketch, "E14.0.61.0", {"start": v(464.82, 0) * mm, "end": v(472.44, 0) * mm});
            skArc(sketch, "E14.3.61.0", {"start": v(470.8, 6.5) * mm, "mid": v(468.63, 7.62) * mm, "end": v(466.46, 6.5) * mm});
            skLineSegment(sketch, "E14.7.61.0", {"start": v(470.8, 6.5) * mm, "end": v(471.46, 5.58) * mm});
            skArc(sketch, "E14.10.61.0", {"start": v(464.82, 5.08) * mm, "mid": v(465.37, 5.21) * mm, "end": v(465.8, 5.58) * mm});
            skPoint(sketch, "E14.14.61.0", {"position": v(471.24, 6.28) * mm});
            skLineSegment(sketch, "E14.15.61.0", {"start": v(465.8, 5.58) * mm, "end": v(466.46, 6.5) * mm});
            skArc(sketch, "E14.18.61.0", {"start": v(471.46, 5.58) * mm, "mid": v(471.9, 5.21) * mm, "end": v(472.44, 5.08) * mm});
            skPoint(sketch, "E14.22.61.0", {"position": v(466.02, 6.28) * mm});
            skLineSegment(sketch, "E14.0.62.0", {"start": v(472.44, 0) * mm, "end": v(480.06, 0) * mm});
            skArc(sketch, "E14.3.62.0", {"start": v(478.42, 6.5) * mm, "mid": v(476.25, 7.62) * mm, "end": v(474.08, 6.5) * mm});
            skLineSegment(sketch, "E14.7.62.0", {"start": v(478.42, 6.5) * mm, "end": v(479.08, 5.58) * mm});
            skArc(sketch, "E14.10.62.0", {"start": v(472.44, 5.08) * mm, "mid": v(472.99, 5.21) * mm, "end": v(473.42, 5.58) * mm});
            skPoint(sketch, "E14.14.62.0", {"position": v(478.86, 6.28) * mm});
            skLineSegment(sketch, "E14.15.62.0", {"start": v(473.42, 5.58) * mm, "end": v(474.08, 6.5) * mm});
            skArc(sketch, "E14.18.62.0", {"start": v(479.08, 5.58) * mm, "mid": v(479.51, 5.21) * mm, "end": v(480.06, 5.08) * mm});
            skPoint(sketch, "E14.22.62.0", {"position": v(473.64, 6.28) * mm});
            skLineSegment(sketch, "E14.0.63.0", {"start": v(480.06, 0) * mm, "end": v(487.68, 0) * mm});
            skArc(sketch, "E14.3.63.0", {"start": v(486.04, 6.5) * mm, "mid": v(483.87, 7.62) * mm, "end": v(481.7, 6.5) * mm});
            skLineSegment(sketch, "E14.7.63.0", {"start": v(486.04, 6.5) * mm, "end": v(486.7, 5.58) * mm});
            skArc(sketch, "E14.10.63.0", {"start": v(480.06, 5.08) * mm, "mid": v(480.6, 5.21) * mm, "end": v(481.04, 5.58) * mm});
            skPoint(sketch, "E14.14.63.0", {"position": v(486.48, 6.28) * mm});
            skLineSegment(sketch, "E14.15.63.0", {"start": v(481.04, 5.58) * mm, "end": v(481.7, 6.5) * mm});
            skArc(sketch, "E14.18.63.0", {"start": v(486.7, 5.58) * mm, "mid": v(487.13, 5.21) * mm, "end": v(487.68, 5.08) * mm});
            skPoint(sketch, "E14.22.63.0", {"position": v(481.26, 6.28) * mm});
            skLineSegment(sketch, "E14.0.64.0", {"start": v(487.68, 0) * mm, "end": v(495.3, 0) * mm});
            skArc(sketch, "E14.3.64.0", {"start": v(493.66, 6.5) * mm, "mid": v(491.5, 7.62) * mm, "end": v(489.32, 6.5) * mm});
            skLineSegment(sketch, "E14.7.64.0", {"start": v(493.66, 6.5) * mm, "end": v(494.32, 5.58) * mm});
            skArc(sketch, "E14.10.64.0", {"start": v(487.68, 5.08) * mm, "mid": v(488.23, 5.21) * mm, "end": v(488.66, 5.58) * mm});
            skPoint(sketch, "E14.14.64.0", {"position": v(494.1, 6.28) * mm});
            skLineSegment(sketch, "E14.15.64.0", {"start": v(488.66, 5.58) * mm, "end": v(489.32, 6.5) * mm});
            skArc(sketch, "E14.18.64.0", {"start": v(494.32, 5.58) * mm, "mid": v(494.75, 5.21) * mm, "end": v(495.3, 5.08) * mm});
            skPoint(sketch, "E14.22.64.0", {"position": v(488.88, 6.28) * mm});
            skLineSegment(sketch, "E14.0.65.0", {"start": v(495.3, 0) * mm, "end": v(502.92, 0) * mm});
            skArc(sketch, "E14.3.65.0", {"start": v(501.28, 6.5) * mm, "mid": v(499.1, 7.62) * mm, "end": v(496.94, 6.5) * mm});
            skLineSegment(sketch, "E14.7.65.0", {"start": v(501.28, 6.5) * mm, "end": v(501.94, 5.58) * mm});
            skArc(sketch, "E14.10.65.0", {"start": v(495.3, 5.08) * mm, "mid": v(495.85, 5.21) * mm, "end": v(496.28, 5.58) * mm});
            skPoint(sketch, "E14.14.65.0", {"position": v(501.72, 6.28) * mm});
            skLineSegment(sketch, "E14.15.65.0", {"start": v(496.28, 5.58) * mm, "end": v(496.94, 6.5) * mm});
            skArc(sketch, "E14.18.65.0", {"start": v(501.94, 5.58) * mm, "mid": v(502.37, 5.21) * mm, "end": v(502.92, 5.08) * mm});
            skPoint(sketch, "E14.22.65.0", {"position": v(496.5, 6.28) * mm});
            skLineSegment(sketch, "E14.0.66.0", {"start": v(502.92, 0) * mm, "end": v(510.54, 0) * mm});
            skArc(sketch, "E14.3.66.0", {"start": v(508.9, 6.5) * mm, "mid": v(506.73, 7.62) * mm, "end": v(504.56, 6.5) * mm});
            skLineSegment(sketch, "E14.7.66.0", {"start": v(508.9, 6.5) * mm, "end": v(509.56, 5.58) * mm});
            skArc(sketch, "E14.10.66.0", {"start": v(502.92, 5.08) * mm, "mid": v(503.47, 5.21) * mm, "end": v(503.9, 5.58) * mm});
            skPoint(sketch, "E14.14.66.0", {"position": v(509.34, 6.28) * mm});
            skLineSegment(sketch, "E14.15.66.0", {"start": v(503.9, 5.58) * mm, "end": v(504.56, 6.5) * mm});
            skArc(sketch, "E14.18.66.0", {"start": v(509.56, 5.58) * mm, "mid": v(510, 5.21) * mm, "end": v(510.54, 5.08) * mm});
            skPoint(sketch, "E14.22.66.0", {"position": v(504.12, 6.28) * mm});
            skLineSegment(sketch, "E14.0.67.0", {"start": v(510.54, 0) * mm, "end": v(518.16, 0) * mm});
            skArc(sketch, "E14.3.67.0", {"start": v(516.52, 6.5) * mm, "mid": v(514.35, 7.62) * mm, "end": v(512.18, 6.5) * mm});
            skLineSegment(sketch, "E14.7.67.0", {"start": v(516.52, 6.5) * mm, "end": v(517.18, 5.58) * mm});
            skArc(sketch, "E14.10.67.0", {"start": v(510.54, 5.08) * mm, "mid": v(511.09, 5.21) * mm, "end": v(511.52, 5.58) * mm});
            skPoint(sketch, "E14.14.67.0", {"position": v(516.96, 6.28) * mm});
            skLineSegment(sketch, "E14.15.67.0", {"start": v(511.52, 5.58) * mm, "end": v(512.18, 6.5) * mm});
            skArc(sketch, "E14.18.67.0", {"start": v(517.18, 5.58) * mm, "mid": v(517.61, 5.21) * mm, "end": v(518.16, 5.08) * mm});
            skPoint(sketch, "E14.22.67.0", {"position": v(511.74, 6.28) * mm});
            skLineSegment(sketch, "E14.0.68.0", {"start": v(518.16, 0) * mm, "end": v(525.78, 0) * mm});
            skArc(sketch, "E14.3.68.0", {"start": v(524.14, 6.5) * mm, "mid": v(521.97, 7.62) * mm, "end": v(519.8, 6.5) * mm});
            skLineSegment(sketch, "E14.7.68.0", {"start": v(524.14, 6.5) * mm, "end": v(524.8, 5.58) * mm});
            skArc(sketch, "E14.10.68.0", {"start": v(518.16, 5.08) * mm, "mid": v(518.7, 5.21) * mm, "end": v(519.14, 5.58) * mm});
            skPoint(sketch, "E14.14.68.0", {"position": v(524.58, 6.28) * mm});
            skLineSegment(sketch, "E14.15.68.0", {"start": v(519.14, 5.58) * mm, "end": v(519.8, 6.5) * mm});
            skArc(sketch, "E14.18.68.0", {"start": v(524.8, 5.58) * mm, "mid": v(525.23, 5.21) * mm, "end": v(525.78, 5.08) * mm});
            skPoint(sketch, "E14.22.68.0", {"position": v(519.36, 6.28) * mm});
            skLineSegment(sketch, "E14.0.69.0", {"start": v(525.78, 0) * mm, "end": v(533.4, 0) * mm});
            skArc(sketch, "E14.3.69.0", {"start": v(531.76, 6.5) * mm, "mid": v(529.6, 7.62) * mm, "end": v(527.42, 6.5) * mm});
            skLineSegment(sketch, "E14.7.69.0", {"start": v(531.76, 6.5) * mm, "end": v(532.42, 5.58) * mm});
            skArc(sketch, "E14.10.69.0", {"start": v(525.78, 5.08) * mm, "mid": v(526.33, 5.21) * mm, "end": v(526.76, 5.58) * mm});
            skPoint(sketch, "E14.14.69.0", {"position": v(532.2, 6.28) * mm});
            skLineSegment(sketch, "E14.15.69.0", {"start": v(526.76, 5.58) * mm, "end": v(527.42, 6.5) * mm});
            skArc(sketch, "E14.18.69.0", {"start": v(532.42, 5.58) * mm, "mid": v(532.85, 5.21) * mm, "end": v(533.4, 5.08) * mm});
            skPoint(sketch, "E14.22.69.0", {"position": v(526.98, 6.28) * mm});
            skLineSegment(sketch, "E14.0.70.0", {"start": v(533.4, 0) * mm, "end": v(541.02, 0) * mm});
            skArc(sketch, "E14.3.70.0", {"start": v(539.38, 6.5) * mm, "mid": v(537.2, 7.62) * mm, "end": v(535.04, 6.5) * mm});
            skLineSegment(sketch, "E14.7.70.0", {"start": v(539.38, 6.5) * mm, "end": v(540.04, 5.58) * mm});
            skArc(sketch, "E14.10.70.0", {"start": v(533.4, 5.08) * mm, "mid": v(533.95, 5.21) * mm, "end": v(534.38, 5.58) * mm});
            skPoint(sketch, "E14.14.70.0", {"position": v(539.82, 6.28) * mm});
            skLineSegment(sketch, "E14.15.70.0", {"start": v(534.38, 5.58) * mm, "end": v(535.04, 6.5) * mm});
            skArc(sketch, "E14.18.70.0", {"start": v(540.04, 5.58) * mm, "mid": v(540.47, 5.21) * mm, "end": v(541.02, 5.08) * mm});
            skPoint(sketch, "E14.22.70.0", {"position": v(534.6, 6.28) * mm});
            skLineSegment(sketch, "E14.0.71.0", {"start": v(541.02, 0) * mm, "end": v(548.64, 0) * mm});
            skArc(sketch, "E14.3.71.0", {"start": v(547, 6.5) * mm, "mid": v(544.83, 7.62) * mm, "end": v(542.66, 6.5) * mm});
            skLineSegment(sketch, "E14.7.71.0", {"start": v(547, 6.5) * mm, "end": v(547.66, 5.58) * mm});
            skArc(sketch, "E14.10.71.0", {"start": v(541.02, 5.08) * mm, "mid": v(541.57, 5.21) * mm, "end": v(542, 5.58) * mm});
            skPoint(sketch, "E14.14.71.0", {"position": v(547.44, 6.28) * mm});
            skLineSegment(sketch, "E14.15.71.0", {"start": v(542, 5.58) * mm, "end": v(542.66, 6.5) * mm});
            skArc(sketch, "E14.18.71.0", {"start": v(547.66, 5.58) * mm, "mid": v(548.1, 5.21) * mm, "end": v(548.64, 5.08) * mm});
            skPoint(sketch, "E14.22.71.0", {"position": v(542.22, 6.28) * mm});
            skLineSegment(sketch, "E14.0.72.0", {"start": v(548.64, 0) * mm, "end": v(556.26, 0) * mm});
            skArc(sketch, "E14.3.72.0", {"start": v(554.62, 6.5) * mm, "mid": v(552.45, 7.62) * mm, "end": v(550.28, 6.5) * mm});
            skLineSegment(sketch, "E14.7.72.0", {"start": v(554.62, 6.5) * mm, "end": v(555.28, 5.58) * mm});
            skArc(sketch, "E14.10.72.0", {"start": v(548.64, 5.08) * mm, "mid": v(549.19, 5.21) * mm, "end": v(549.62, 5.58) * mm});
            skPoint(sketch, "E14.14.72.0", {"position": v(555.06, 6.28) * mm});
            skLineSegment(sketch, "E14.15.72.0", {"start": v(549.62, 5.58) * mm, "end": v(550.28, 6.5) * mm});
            skArc(sketch, "E14.18.72.0", {"start": v(555.28, 5.58) * mm, "mid": v(555.71, 5.21) * mm, "end": v(556.26, 5.08) * mm});
            skPoint(sketch, "E14.22.72.0", {"position": v(549.84, 6.28) * mm});
            skLineSegment(sketch, "E14.0.73.0", {"start": v(556.26, 0) * mm, "end": v(563.88, 0) * mm});
            skArc(sketch, "E14.3.73.0", {"start": v(562.24, 6.5) * mm, "mid": v(560.07, 7.62) * mm, "end": v(557.9, 6.5) * mm});
            skLineSegment(sketch, "E14.7.73.0", {"start": v(562.24, 6.5) * mm, "end": v(562.9, 5.58) * mm});
            skArc(sketch, "E14.10.73.0", {"start": v(556.26, 5.08) * mm, "mid": v(556.8, 5.21) * mm, "end": v(557.24, 5.58) * mm});
            skPoint(sketch, "E14.14.73.0", {"position": v(562.68, 6.28) * mm});
            skLineSegment(sketch, "E14.15.73.0", {"start": v(557.24, 5.58) * mm, "end": v(557.9, 6.5) * mm});
            skArc(sketch, "E14.18.73.0", {"start": v(562.9, 5.58) * mm, "mid": v(563.33, 5.21) * mm, "end": v(563.88, 5.08) * mm});
            skPoint(sketch, "E14.22.73.0", {"position": v(557.46, 6.28) * mm});
            skLineSegment(sketch, "E14.0.74.0", {"start": v(563.88, 0) * mm, "end": v(571.5, 0) * mm});
            skArc(sketch, "E14.3.74.0", {"start": v(569.86, 6.5) * mm, "mid": v(567.7, 7.62) * mm, "end": v(565.52, 6.5) * mm});
            skLineSegment(sketch, "E14.7.74.0", {"start": v(569.86, 6.5) * mm, "end": v(570.52, 5.58) * mm});
            skArc(sketch, "E14.10.74.0", {"start": v(563.88, 5.08) * mm, "mid": v(564.43, 5.21) * mm, "end": v(564.86, 5.58) * mm});
            skPoint(sketch, "E14.14.74.0", {"position": v(570.3, 6.28) * mm});
            skLineSegment(sketch, "E14.15.74.0", {"start": v(564.86, 5.58) * mm, "end": v(565.52, 6.5) * mm});
            skArc(sketch, "E14.18.74.0", {"start": v(570.52, 5.58) * mm, "mid": v(570.95, 5.21) * mm, "end": v(571.5, 5.08) * mm});
            skPoint(sketch, "E14.22.74.0", {"position": v(565.08, 6.28) * mm});
            skLineSegment(sketch, "E14.0.75.0", {"start": v(571.5, 0) * mm, "end": v(579.12, 0) * mm});
            skArc(sketch, "E14.3.75.0", {"start": v(577.48, 6.5) * mm, "mid": v(575.31, 7.62) * mm, "end": v(573.14, 6.5) * mm});
            skLineSegment(sketch, "E14.7.75.0", {"start": v(577.48, 6.5) * mm, "end": v(578.14, 5.58) * mm});
            skArc(sketch, "E14.10.75.0", {"start": v(571.5, 5.08) * mm, "mid": v(572.05, 5.21) * mm, "end": v(572.48, 5.58) * mm});
            skPoint(sketch, "E14.14.75.0", {"position": v(577.92, 6.28) * mm});
            skLineSegment(sketch, "E14.15.75.0", {"start": v(572.48, 5.58) * mm, "end": v(573.14, 6.5) * mm});
            skArc(sketch, "E14.18.75.0", {"start": v(578.14, 5.58) * mm, "mid": v(578.57, 5.21) * mm, "end": v(579.12, 5.08) * mm});
            skPoint(sketch, "E14.22.75.0", {"position": v(572.7, 6.28) * mm});
            skLineSegment(sketch, "E14.0.76.0", {"start": v(579.12, 0) * mm, "end": v(586.74, 0) * mm});
            skArc(sketch, "E14.3.76.0", {"start": v(585.1, 6.5) * mm, "mid": v(582.93, 7.62) * mm, "end": v(580.76, 6.5) * mm});
            skLineSegment(sketch, "E14.7.76.0", {"start": v(585.1, 6.5) * mm, "end": v(585.76, 5.58) * mm});
            skArc(sketch, "E14.10.76.0", {"start": v(579.12, 5.08) * mm, "mid": v(579.67, 5.21) * mm, "end": v(580.1, 5.58) * mm});
            skPoint(sketch, "E14.14.76.0", {"position": v(585.54, 6.28) * mm});
            skLineSegment(sketch, "E14.15.76.0", {"start": v(580.1, 5.58) * mm, "end": v(580.76, 6.5) * mm});
            skArc(sketch, "E14.18.76.0", {"start": v(585.76, 5.58) * mm, "mid": v(586.2, 5.21) * mm, "end": v(586.74, 5.08) * mm});
            skPoint(sketch, "E14.22.76.0", {"position": v(580.32, 6.28) * mm});
            skLineSegment(sketch, "E14.0.77.0", {"start": v(586.74, 0) * mm, "end": v(594.36, 0) * mm});
            skArc(sketch, "E14.3.77.0", {"start": v(592.72, 6.5) * mm, "mid": v(590.55, 7.62) * mm, "end": v(588.38, 6.5) * mm});
            skLineSegment(sketch, "E14.7.77.0", {"start": v(592.72, 6.5) * mm, "end": v(593.38, 5.58) * mm});
            skArc(sketch, "E14.10.77.0", {"start": v(586.74, 5.08) * mm, "mid": v(587.29, 5.21) * mm, "end": v(587.72, 5.58) * mm});
            skPoint(sketch, "E14.14.77.0", {"position": v(593.16, 6.28) * mm});
            skLineSegment(sketch, "E14.15.77.0", {"start": v(587.72, 5.58) * mm, "end": v(588.38, 6.5) * mm});
            skArc(sketch, "E14.18.77.0", {"start": v(593.38, 5.58) * mm, "mid": v(593.81, 5.21) * mm, "end": v(594.36, 5.08) * mm});
            skPoint(sketch, "E14.22.77.0", {"position": v(587.94, 6.28) * mm});
            skLineSegment(sketch, "E14.0.78.0", {"start": v(594.36, 0) * mm, "end": v(601.98, 0) * mm});
            skArc(sketch, "E14.3.78.0", {"start": v(600.34, 6.5) * mm, "mid": v(598.17, 7.62) * mm, "end": v(596, 6.5) * mm});
            skLineSegment(sketch, "E14.7.78.0", {"start": v(600.34, 6.5) * mm, "end": v(601, 5.58) * mm});
            skArc(sketch, "E14.10.78.0", {"start": v(594.36, 5.08) * mm, "mid": v(594.9, 5.21) * mm, "end": v(595.34, 5.58) * mm});
            skPoint(sketch, "E14.14.78.0", {"position": v(600.78, 6.28) * mm});
            skLineSegment(sketch, "E14.15.78.0", {"start": v(595.34, 5.58) * mm, "end": v(596, 6.5) * mm});
            skArc(sketch, "E14.18.78.0", {"start": v(601, 5.58) * mm, "mid": v(601.43, 5.21) * mm, "end": v(601.98, 5.08) * mm});
            skPoint(sketch, "E14.22.78.0", {"position": v(595.56, 6.28) * mm});
            skLineSegment(sketch, "E14.0.79.0", {"start": v(601.98, 0) * mm, "end": v(609.6, 0) * mm});
            skArc(sketch, "E14.3.79.0", {"start": v(607.96, 6.5) * mm, "mid": v(605.8, 7.62) * mm, "end": v(603.62, 6.5) * mm});
            skLineSegment(sketch, "E14.7.79.0", {"start": v(607.96, 6.5) * mm, "end": v(608.62, 5.58) * mm});
            skArc(sketch, "E14.10.79.0", {"start": v(601.98, 5.08) * mm, "mid": v(602.53, 5.21) * mm, "end": v(602.96, 5.58) * mm});
            skPoint(sketch, "E14.14.79.0", {"position": v(608.4, 6.28) * mm});
            skLineSegment(sketch, "E14.15.79.0", {"start": v(602.96, 5.58) * mm, "end": v(603.62, 6.5) * mm});
            skArc(sketch, "E14.18.79.0", {"start": v(608.62, 5.58) * mm, "mid": v(609.05, 5.21) * mm, "end": v(609.6, 5.08) * mm});
            skPoint(sketch, "E14.22.79.0", {"position": v(603.18, 6.28) * mm});
            skLineSegment(sketch, "E14.0.80.0", {"start": v(609.6, 0) * mm, "end": v(617.22, 0) * mm});
            skArc(sketch, "E14.3.80.0", {"start": v(615.58, 6.5) * mm, "mid": v(613.41, 7.62) * mm, "end": v(611.24, 6.5) * mm});
            skLineSegment(sketch, "E14.7.80.0", {"start": v(615.58, 6.5) * mm, "end": v(616.24, 5.58) * mm});
            skArc(sketch, "E14.10.80.0", {"start": v(609.6, 5.08) * mm, "mid": v(610.15, 5.21) * mm, "end": v(610.58, 5.58) * mm});
            skPoint(sketch, "E14.14.80.0", {"position": v(616.02, 6.28) * mm});
            skLineSegment(sketch, "E14.15.80.0", {"start": v(610.58, 5.58) * mm, "end": v(611.24, 6.5) * mm});
            skArc(sketch, "E14.18.80.0", {"start": v(616.24, 5.58) * mm, "mid": v(616.67, 5.21) * mm, "end": v(617.22, 5.08) * mm});
            skPoint(sketch, "E14.22.80.0", {"position": v(610.8, 6.28) * mm});
            skLineSegment(sketch, "E14.0.81.0", {"start": v(617.22, 0) * mm, "end": v(624.84, 0) * mm});
            skArc(sketch, "E14.3.81.0", {"start": v(623.2, 6.5) * mm, "mid": v(621.03, 7.62) * mm, "end": v(618.86, 6.5) * mm});
            skLineSegment(sketch, "E14.7.81.0", {"start": v(623.2, 6.5) * mm, "end": v(623.86, 5.58) * mm});
            skArc(sketch, "E14.10.81.0", {"start": v(617.22, 5.08) * mm, "mid": v(617.77, 5.21) * mm, "end": v(618.2, 5.58) * mm});
            skPoint(sketch, "E14.14.81.0", {"position": v(623.64, 6.28) * mm});
            skLineSegment(sketch, "E14.15.81.0", {"start": v(618.2, 5.58) * mm, "end": v(618.86, 6.5) * mm});
            skArc(sketch, "E14.18.81.0", {"start": v(623.86, 5.58) * mm, "mid": v(624.3, 5.21) * mm, "end": v(624.84, 5.08) * mm});
            skPoint(sketch, "E14.22.81.0", {"position": v(618.42, 6.28) * mm});
            skLineSegment(sketch, "E14.0.82.0", {"start": v(624.84, 0) * mm, "end": v(632.46, 0) * mm});
            skArc(sketch, "E14.3.82.0", {"start": v(630.82, 6.5) * mm, "mid": v(628.65, 7.62) * mm, "end": v(626.48, 6.5) * mm});
            skLineSegment(sketch, "E14.7.82.0", {"start": v(630.82, 6.5) * mm, "end": v(631.48, 5.58) * mm});
            skArc(sketch, "E14.10.82.0", {"start": v(624.84, 5.08) * mm, "mid": v(625.39, 5.21) * mm, "end": v(625.82, 5.58) * mm});
            skPoint(sketch, "E14.14.82.0", {"position": v(631.26, 6.28) * mm});
            skLineSegment(sketch, "E14.15.82.0", {"start": v(625.82, 5.58) * mm, "end": v(626.48, 6.5) * mm});
            skArc(sketch, "E14.18.82.0", {"start": v(631.48, 5.58) * mm, "mid": v(631.91, 5.21) * mm, "end": v(632.46, 5.08) * mm});
            skPoint(sketch, "E14.22.82.0", {"position": v(626.04, 6.28) * mm});
            skLineSegment(sketch, "E14.0.83.0", {"start": v(632.46, 0) * mm, "end": v(640.08, 0) * mm});
            skArc(sketch, "E14.3.83.0", {"start": v(638.44, 6.5) * mm, "mid": v(636.27, 7.62) * mm, "end": v(634.1, 6.5) * mm});
            skLineSegment(sketch, "E14.7.83.0", {"start": v(638.44, 6.5) * mm, "end": v(639.1, 5.58) * mm});
            skArc(sketch, "E14.10.83.0", {"start": v(632.46, 5.08) * mm, "mid": v(633, 5.21) * mm, "end": v(633.44, 5.58) * mm});
            skPoint(sketch, "E14.14.83.0", {"position": v(638.88, 6.28) * mm});
            skLineSegment(sketch, "E14.15.83.0", {"start": v(633.44, 5.58) * mm, "end": v(634.1, 6.5) * mm});
            skArc(sketch, "E14.18.83.0", {"start": v(639.1, 5.58) * mm, "mid": v(639.53, 5.21) * mm, "end": v(640.08, 5.08) * mm});
            skPoint(sketch, "E14.22.83.0", {"position": v(633.66, 6.28) * mm});
            skLineSegment(sketch, "E14.0.84.0", {"start": v(640.08, 0) * mm, "end": v(647.7, 0) * mm});
            skArc(sketch, "E14.3.84.0", {"start": v(646.06, 6.5) * mm, "mid": v(643.9, 7.62) * mm, "end": v(641.72, 6.5) * mm});
            skLineSegment(sketch, "E14.7.84.0", {"start": v(646.06, 6.5) * mm, "end": v(646.72, 5.58) * mm});
            skArc(sketch, "E14.10.84.0", {"start": v(640.08, 5.08) * mm, "mid": v(640.63, 5.21) * mm, "end": v(641.06, 5.58) * mm});
            skPoint(sketch, "E14.14.84.0", {"position": v(646.5, 6.28) * mm});
            skLineSegment(sketch, "E14.15.84.0", {"start": v(641.06, 5.58) * mm, "end": v(641.72, 6.5) * mm});
            skArc(sketch, "E14.18.84.0", {"start": v(646.72, 5.58) * mm, "mid": v(647.15, 5.21) * mm, "end": v(647.7, 5.08) * mm});
            skPoint(sketch, "E14.22.84.0", {"position": v(641.28, 6.28) * mm});
            skLineSegment(sketch, "E15", {"start": v(647.7, 0) * mm, "end": v(647.7, 5.08) * mm});
            skLineSegment(sketch, "E16", {"start": v(0, 0) * mm, "end": v(0, 5.08) * mm});
            skSolve(sketch);
        }
        {
            var Q0;
            Q0=qSketchRegion(id+"F0",true);
            extrude(context, id + "F1", {"entities" : qUnion([Q0]), "depth" : 12.7 * mm});
        }
    });
